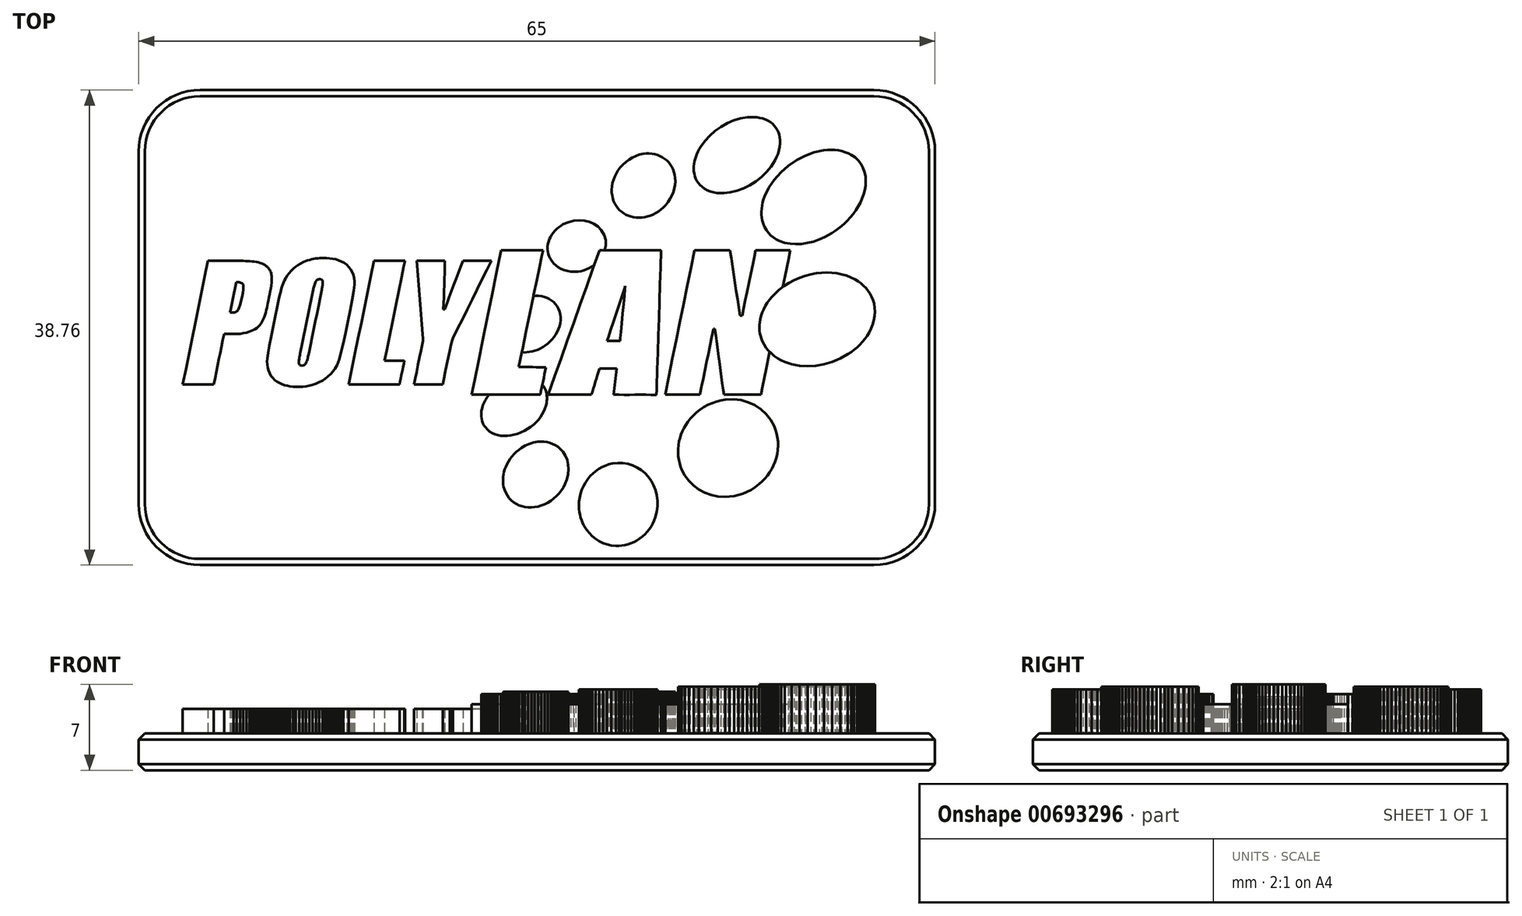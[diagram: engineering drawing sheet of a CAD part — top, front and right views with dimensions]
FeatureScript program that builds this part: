
annotation { "Feature Type Name" : "Feature", "Feature Type Description" : "" }
export const myFeature = defineFeature(function(context is Context, id is Id, definition is map)
    precondition{}
    {
        {
            var Q0;
            Q0=qCreatedBy(makeId("Top.planeOp"),FACE);
            var sketch = newSketch(context, id + "F0", { "sketchPlane" : qUnion([Q0])});
            skLineSegment(sketch, "E0.bottom", {"start": v(-32.5, 0) * mm, "end": v(32.5, 0) * mm});
            skLineSegment(sketch, "E0.top", {"start": v(-32.5, -38.76) * mm, "end": v(32.5, -38.76) * mm});
            skLineSegment(sketch, "E0.left", {"start": v(-32.5, 0) * mm, "end": v(-32.5, -38.76) * mm});
            skLineSegment(sketch, "E0.right", {"start": v(32.5, 0) * mm, "end": v(32.5, -38.76) * mm});
            skSolve(sketch);
        }
        {
            var Q0;
            Q0 = qSketchRegion(id + "F0", true);
            extrude(context, id + "F1", {"entities" : qUnion([Q0]), "depth" : 3 * mm, "offsetDistance" : 25 * mm});
        }
        {
            var Q0;
            Q0=makeQuery(id+"F1.opExtrude","CAP_FACE",FACE,{"disambiguationData":[OSD([sQuery(id+"F0.wireOp",EDGE,"E0.bottom"),sQuery(id+"F0.wireOp",EDGE,"E0.top"),sQuery(id+"F0.wireOp",EDGE,"E0.left"),sQuery(id+"F0.wireOp",EDGE,"E0.right")])],"isStart":false});
            var sketch = newSketch(context, id + "F2", { "sketchPlane" : qUnion([Q0])});
            skLineSegment(sketch, "E1", {"start": v(2.14, -10.96) * mm, "end": v(2.58, -10.77) * mm});
            skLineSegment(sketch, "E2", {"start": v(2.58, -10.77) * mm, "end": v(3.02, -10.66) * mm});
            skLineSegment(sketch, "E3", {"start": v(3.02, -10.66) * mm, "end": v(3.45, -10.62) * mm});
            skLineSegment(sketch, "E4", {"start": v(3.45, -10.62) * mm, "end": v(3.88, -10.66) * mm});
            skLineSegment(sketch, "E5", {"start": v(3.88, -10.66) * mm, "end": v(4.28, -10.76) * mm});
            skLineSegment(sketch, "E6", {"start": v(4.28, -10.76) * mm, "end": v(4.65, -10.92) * mm});
            skLineSegment(sketch, "E7", {"start": v(4.65, -10.92) * mm, "end": v(4.98, -11.14) * mm});
            skLineSegment(sketch, "E8", {"start": v(4.98, -11.14) * mm, "end": v(5.25, -11.42) * mm});
            skLineSegment(sketch, "E9", {"start": v(5.25, -11.42) * mm, "end": v(5.5, -11.83) * mm});
            skLineSegment(sketch, "E10", {"start": v(5.5, -11.83) * mm, "end": v(5.6, -12.25) * mm});
            skLineSegment(sketch, "E11", {"start": v(5.6, -12.25) * mm, "end": v(5.62, -12.68) * mm});
            skLineSegment(sketch, "E12", {"start": v(5.62, -12.68) * mm, "end": v(5.54, -13.1) * mm});
            skLineSegment(sketch, "E13", {"start": v(5.54, -13.1) * mm, "end": v(5.37, -13.49) * mm});
            skLineSegment(sketch, "E14", {"start": v(5.37, -13.49) * mm, "end": v(5.13, -13.85) * mm});
            skLineSegment(sketch, "E15", {"start": v(5.13, -13.85) * mm, "end": v(4.84, -14.16) * mm});
            skLineSegment(sketch, "E16", {"start": v(4.84, -14.16) * mm, "end": v(4.5, -14.4) * mm});
            skLineSegment(sketch, "E17", {"start": v(4.5, -14.4) * mm, "end": v(4.25, -14.54) * mm});
            skLineSegment(sketch, "E18", {"start": v(4.25, -14.54) * mm, "end": v(4.02, -14.64) * mm});
            skLineSegment(sketch, "E19", {"start": v(4.02, -14.64) * mm, "end": v(3.8, -14.72) * mm});
            skLineSegment(sketch, "E20", {"start": v(3.8, -14.72) * mm, "end": v(3.59, -14.77) * mm});
            skLineSegment(sketch, "E21", {"start": v(3.59, -14.77) * mm, "end": v(3.38, -14.8) * mm});
            skLineSegment(sketch, "E22", {"start": v(3.38, -14.8) * mm, "end": v(3.17, -14.82) * mm});
            skLineSegment(sketch, "E23", {"start": v(3.17, -14.82) * mm, "end": v(2.96, -14.82) * mm});
            skLineSegment(sketch, "E24", {"start": v(2.96, -14.82) * mm, "end": v(2.75, -14.8) * mm});
            skLineSegment(sketch, "E25", {"start": v(2.75, -14.8) * mm, "end": v(2.49, -14.76) * mm});
            skLineSegment(sketch, "E26", {"start": v(2.49, -14.76) * mm, "end": v(2.23, -14.68) * mm});
            skLineSegment(sketch, "E27", {"start": v(2.23, -14.68) * mm, "end": v(1.99, -14.59) * mm});
            skLineSegment(sketch, "E28", {"start": v(1.99, -14.59) * mm, "end": v(1.76, -14.46) * mm});
            skLineSegment(sketch, "E29", {"start": v(1.76, -14.46) * mm, "end": v(1.55, -14.31) * mm});
            skLineSegment(sketch, "E30", {"start": v(1.55, -14.31) * mm, "end": v(1.37, -14.14) * mm});
            skLineSegment(sketch, "E31", {"start": v(1.37, -14.14) * mm, "end": v(1.2, -13.94) * mm});
            skLineSegment(sketch, "E32", {"start": v(1.2, -13.94) * mm, "end": v(1.07, -13.73) * mm});
            skLineSegment(sketch, "E33", {"start": v(1.07, -13.73) * mm, "end": v(1, -13.55) * mm});
            skLineSegment(sketch, "E34", {"start": v(1, -13.55) * mm, "end": v(0.93, -13.37) * mm});
            skLineSegment(sketch, "E35", {"start": v(0.93, -13.37) * mm, "end": v(0.89, -13.18) * mm});
            skLineSegment(sketch, "E36", {"start": v(0.89, -13.18) * mm, "end": v(0.87, -12.98) * mm});
            skLineSegment(sketch, "E37", {"start": v(0.87, -12.98) * mm, "end": v(0.87, -12.78) * mm});
            skLineSegment(sketch, "E38", {"start": v(0.87, -12.78) * mm, "end": v(0.9, -12.58) * mm});
            skLineSegment(sketch, "E39", {"start": v(0.9, -12.58) * mm, "end": v(0.94, -12.37) * mm});
            skLineSegment(sketch, "E40", {"start": v(0.94, -12.37) * mm, "end": v(1.02, -12.17) * mm});
            skLineSegment(sketch, "E41", {"start": v(1.02, -12.17) * mm, "end": v(1.1, -11.98) * mm});
            skLineSegment(sketch, "E42", {"start": v(1.1, -11.98) * mm, "end": v(1.2, -11.8) * mm});
            skLineSegment(sketch, "E43", {"start": v(1.2, -11.8) * mm, "end": v(1.33, -11.63) * mm});
            skLineSegment(sketch, "E44", {"start": v(1.33, -11.63) * mm, "end": v(1.47, -11.47) * mm});
            skLineSegment(sketch, "E45", {"start": v(1.47, -11.47) * mm, "end": v(1.62, -11.32) * mm});
            skLineSegment(sketch, "E46", {"start": v(1.62, -11.32) * mm, "end": v(1.79, -11.19) * mm});
            skLineSegment(sketch, "E47", {"start": v(1.79, -11.19) * mm, "end": v(1.96, -11.06) * mm});
            skLineSegment(sketch, "E48", {"start": v(1.96, -11.06) * mm, "end": v(2.14, -10.96) * mm});
            skLineSegment(sketch, "E49", {"start": v(-0.1, -16.78) * mm, "end": v(0.14, -16.8) * mm});
            skLineSegment(sketch, "E50", {"start": v(0.14, -16.8) * mm, "end": v(0.37, -16.83) * mm});
            skLineSegment(sketch, "E51", {"start": v(0.37, -16.83) * mm, "end": v(0.6, -16.88) * mm});
            skLineSegment(sketch, "E52", {"start": v(0.6, -16.88) * mm, "end": v(0.8, -16.96) * mm});
            skLineSegment(sketch, "E53", {"start": v(0.8, -16.96) * mm, "end": v(1, -17.06) * mm});
            skLineSegment(sketch, "E54", {"start": v(1, -17.06) * mm, "end": v(1.19, -17.17) * mm});
            skLineSegment(sketch, "E55", {"start": v(1.19, -17.17) * mm, "end": v(1.36, -17.3) * mm});
            skLineSegment(sketch, "E56", {"start": v(1.36, -17.3) * mm, "end": v(1.5, -17.47) * mm});
            skLineSegment(sketch, "E57", {"start": v(1.5, -17.47) * mm, "end": v(1.65, -17.65) * mm});
            skLineSegment(sketch, "E58", {"start": v(1.65, -17.65) * mm, "end": v(1.76, -17.85) * mm});
            skLineSegment(sketch, "E59", {"start": v(1.76, -17.85) * mm, "end": v(1.84, -18.07) * mm});
            skLineSegment(sketch, "E60", {"start": v(1.84, -18.07) * mm, "end": v(1.9, -18.3) * mm});
            skLineSegment(sketch, "E61", {"start": v(1.9, -18.3) * mm, "end": v(1.93, -18.54) * mm});
            skLineSegment(sketch, "E62", {"start": v(1.93, -18.54) * mm, "end": v(1.93, -18.78) * mm});
            skLineSegment(sketch, "E63", {"start": v(1.93, -18.78) * mm, "end": v(1.9, -19.04) * mm});
            skLineSegment(sketch, "E64", {"start": v(1.9, -19.04) * mm, "end": v(1.84, -19.29) * mm});
            skLineSegment(sketch, "E65", {"start": v(1.84, -19.29) * mm, "end": v(1.77, -19.51) * mm});
            skLineSegment(sketch, "E66", {"start": v(1.77, -19.51) * mm, "end": v(1.67, -19.74) * mm});
            skLineSegment(sketch, "E67", {"start": v(1.67, -19.74) * mm, "end": v(1.54, -19.95) * mm});
            skLineSegment(sketch, "E68", {"start": v(1.54, -19.95) * mm, "end": v(1.4, -20.15) * mm});
            skLineSegment(sketch, "E69", {"start": v(1.4, -20.15) * mm, "end": v(1.24, -20.35) * mm});
            skLineSegment(sketch, "E70", {"start": v(1.24, -20.35) * mm, "end": v(1.07, -20.53) * mm});
            skLineSegment(sketch, "E71", {"start": v(1.07, -20.53) * mm, "end": v(0.88, -20.7) * mm});
            skLineSegment(sketch, "E72", {"start": v(0.88, -20.7) * mm, "end": v(0.68, -20.85) * mm});
            skLineSegment(sketch, "E73", {"start": v(0.68, -20.85) * mm, "end": v(0.48, -20.98) * mm});
            skLineSegment(sketch, "E74", {"start": v(0.48, -20.98) * mm, "end": v(0.27, -21.1) * mm});
            skLineSegment(sketch, "E75", {"start": v(0.27, -21.1) * mm, "end": v(0.06, -21.19) * mm});
            skLineSegment(sketch, "E76", {"start": v(0.06, -21.19) * mm, "end": v(-0.16, -21.27) * mm});
            skLineSegment(sketch, "E77", {"start": v(-0.16, -21.27) * mm, "end": v(-0.38, -21.33) * mm});
            skLineSegment(sketch, "E78", {"start": v(-0.38, -21.33) * mm, "end": v(-0.6, -21.37) * mm});
            skLineSegment(sketch, "E79", {"start": v(-0.6, -21.37) * mm, "end": v(-0.82, -21.4) * mm});
            skLineSegment(sketch, "E80", {"start": v(-0.82, -21.4) * mm, "end": v(-1.04, -21.41) * mm});
            skLineSegment(sketch, "E81", {"start": v(-1.04, -21.41) * mm, "end": v(-2.2, -21.3) * mm});
            skLineSegment(sketch, "E82", {"start": v(-2.2, -21.3) * mm, "end": v(-2.99, -20.8) * mm});
            skLineSegment(sketch, "E83", {"start": v(-2.99, -20.8) * mm, "end": v(-3.4, -20.08) * mm});
            skLineSegment(sketch, "E84", {"start": v(-3.4, -20.08) * mm, "end": v(-3.43, -19.23) * mm});
            skLineSegment(sketch, "E85", {"start": v(-3.43, -19.23) * mm, "end": v(-3.12, -18.35) * mm});
            skLineSegment(sketch, "E86", {"start": v(-3.12, -18.35) * mm, "end": v(-2.45, -17.58) * mm});
            skLineSegment(sketch, "E87", {"start": v(-2.45, -17.58) * mm, "end": v(-1.44, -17.02) * mm});
            skLineSegment(sketch, "E88", {"start": v(-1.44, -17.02) * mm, "end": v(-0.1, -16.78) * mm});
            skLineSegment(sketch, "E89", {"start": v(0.68, -24.4) * mm, "end": v(0.73, -24.52) * mm});
            skLineSegment(sketch, "E90", {"start": v(0.73, -24.52) * mm, "end": v(0.77, -24.65) * mm});
            skLineSegment(sketch, "E91", {"start": v(0.77, -24.65) * mm, "end": v(0.8, -24.79) * mm});
            skLineSegment(sketch, "E92", {"start": v(0.8, -24.79) * mm, "end": v(0.81, -24.93) * mm});
            skLineSegment(sketch, "E93", {"start": v(0.81, -24.93) * mm, "end": v(0.82, -25.08) * mm});
            skLineSegment(sketch, "E94", {"start": v(0.82, -25.08) * mm, "end": v(0.82, -25.23) * mm});
            skLineSegment(sketch, "E95", {"start": v(0.82, -25.23) * mm, "end": v(0.8, -25.38) * mm});
            skLineSegment(sketch, "E96", {"start": v(0.8, -25.38) * mm, "end": v(0.79, -25.54) * mm});
            skLineSegment(sketch, "E97", {"start": v(0.79, -25.54) * mm, "end": v(0.73, -25.78) * mm});
            skLineSegment(sketch, "E98", {"start": v(0.73, -25.78) * mm, "end": v(0.65, -26.02) * mm});
            skLineSegment(sketch, "E99", {"start": v(0.65, -26.02) * mm, "end": v(0.55, -26.25) * mm});
            skLineSegment(sketch, "E100", {"start": v(0.55, -26.25) * mm, "end": v(0.43, -26.48) * mm});
            skLineSegment(sketch, "E101", {"start": v(0.43, -26.48) * mm, "end": v(0.28, -26.7) * mm});
            skLineSegment(sketch, "E102", {"start": v(0.28, -26.7) * mm, "end": v(0.12, -26.91) * mm});
            skLineSegment(sketch, "E103", {"start": v(0.12, -26.91) * mm, "end": v(-0.06, -27.1) * mm});
            skLineSegment(sketch, "E104", {"start": v(-0.06, -27.1) * mm, "end": v(-0.26, -27.29) * mm});
            skLineSegment(sketch, "E105", {"start": v(-0.26, -27.29) * mm, "end": v(-0.5, -27.48) * mm});
            skLineSegment(sketch, "E106", {"start": v(-0.5, -27.48) * mm, "end": v(-0.75, -27.66) * mm});
            skLineSegment(sketch, "E107", {"start": v(-0.75, -27.66) * mm, "end": v(-1.02, -27.81) * mm});
            skLineSegment(sketch, "E108", {"start": v(-1.02, -27.81) * mm, "end": v(-1.3, -27.94) * mm});
            skLineSegment(sketch, "E109", {"start": v(-1.3, -27.94) * mm, "end": v(-1.57, -28.05) * mm});
            skLineSegment(sketch, "E110", {"start": v(-1.57, -28.05) * mm, "end": v(-1.85, -28.13) * mm});
            skLineSegment(sketch, "E111", {"start": v(-1.85, -28.13) * mm, "end": v(-2.14, -28.19) * mm});
            skLineSegment(sketch, "E112", {"start": v(-2.14, -28.19) * mm, "end": v(-2.42, -28.22) * mm});
            skLineSegment(sketch, "E113", {"start": v(-2.42, -28.22) * mm, "end": v(-2.68, -28.22) * mm});
            skLineSegment(sketch, "E114", {"start": v(-2.68, -28.22) * mm, "end": v(-2.94, -28.2) * mm});
            skLineSegment(sketch, "E115", {"start": v(-2.94, -28.2) * mm, "end": v(-3.2, -28.16) * mm});
            skLineSegment(sketch, "E116", {"start": v(-3.2, -28.16) * mm, "end": v(-3.43, -28.08) * mm});
            skLineSegment(sketch, "E117", {"start": v(-3.43, -28.08) * mm, "end": v(-3.65, -27.98) * mm});
            skLineSegment(sketch, "E118", {"start": v(-3.65, -27.98) * mm, "end": v(-3.86, -27.86) * mm});
            skLineSegment(sketch, "E119", {"start": v(-3.86, -27.86) * mm, "end": v(-4.04, -27.71) * mm});
            skLineSegment(sketch, "E120", {"start": v(-4.04, -27.71) * mm, "end": v(-4.2, -27.53) * mm});
            skLineSegment(sketch, "E121", {"start": v(-4.2, -27.53) * mm, "end": v(-4.31, -27.38) * mm});
            skLineSegment(sketch, "E122", {"start": v(-4.31, -27.38) * mm, "end": v(-4.4, -27.2) * mm});
            skLineSegment(sketch, "E123", {"start": v(-4.4, -27.2) * mm, "end": v(-4.47, -27.02) * mm});
            skLineSegment(sketch, "E124", {"start": v(-4.47, -27.02) * mm, "end": v(-4.52, -26.82) * mm});
            skLineSegment(sketch, "E125", {"start": v(-4.52, -26.82) * mm, "end": v(-4.54, -26.62) * mm});
            skLineSegment(sketch, "E126", {"start": v(-4.54, -26.62) * mm, "end": v(-4.54, -26.4) * mm});
            skLineSegment(sketch, "E127", {"start": v(-4.54, -26.4) * mm, "end": v(-4.52, -26.2) * mm});
            skLineSegment(sketch, "E128", {"start": v(-4.52, -26.2) * mm, "end": v(-4.48, -25.98) * mm});
            skLineSegment(sketch, "E129", {"start": v(-4.48, -25.98) * mm, "end": v(-4.44, -25.85) * mm});
            skLineSegment(sketch, "E130", {"start": v(-4.44, -25.85) * mm, "end": v(-4.4, -25.72) * mm});
            skLineSegment(sketch, "E131", {"start": v(-4.4, -25.72) * mm, "end": v(-4.35, -25.6) * mm});
            skLineSegment(sketch, "E132", {"start": v(-4.35, -25.6) * mm, "end": v(-4.29, -25.47) * mm});
            skLineSegment(sketch, "E133", {"start": v(-4.29, -25.47) * mm, "end": v(-4.22, -25.34) * mm});
            skLineSegment(sketch, "E134", {"start": v(-4.22, -25.34) * mm, "end": v(-4.15, -25.22) * mm});
            skLineSegment(sketch, "E135", {"start": v(-4.15, -25.22) * mm, "end": v(-4.08, -25.1) * mm});
            skLineSegment(sketch, "E136", {"start": v(-4.08, -25.1) * mm, "end": v(-4, -24.98) * mm});
            skLineSegment(sketch, "E137", {"start": v(-4, -24.98) * mm, "end": v(-3.7, -24.66) * mm});
            skLineSegment(sketch, "E138", {"start": v(-3.7, -24.66) * mm, "end": v(-3.35, -24.37) * mm});
            skLineSegment(sketch, "E139", {"start": v(-3.35, -24.37) * mm, "end": v(-3, -24.13) * mm});
            skLineSegment(sketch, "E140", {"start": v(-3, -24.13) * mm, "end": v(-2.64, -23.92) * mm});
            skLineSegment(sketch, "E141", {"start": v(-2.64, -23.92) * mm, "end": v(-2.28, -23.76) * mm});
            skLineSegment(sketch, "E142", {"start": v(-2.28, -23.76) * mm, "end": v(-1.95, -23.64) * mm});
            skLineSegment(sketch, "E143", {"start": v(-1.95, -23.64) * mm, "end": v(-1.66, -23.57) * mm});
            skLineSegment(sketch, "E144", {"start": v(-1.66, -23.57) * mm, "end": v(-1.4, -23.55) * mm});
            skLineSegment(sketch, "E145", {"start": v(-1.4, -23.55) * mm, "end": v(-0.8, -23.57) * mm});
            skLineSegment(sketch, "E146", {"start": v(-0.8, -23.57) * mm, "end": v(-0.33, -23.64) * mm});
            skLineSegment(sketch, "E147", {"start": v(-0.33, -23.64) * mm, "end": v(0.02, -23.74) * mm});
            skLineSegment(sketch, "E148", {"start": v(0.02, -23.74) * mm, "end": v(0.26, -23.87) * mm});
            skLineSegment(sketch, "E149", {"start": v(0.26, -23.87) * mm, "end": v(0.42, -24) * mm});
            skLineSegment(sketch, "E150", {"start": v(0.42, -24) * mm, "end": v(0.53, -24.15) * mm});
            skLineSegment(sketch, "E151", {"start": v(0.53, -24.15) * mm, "end": v(0.61, -24.28) * mm});
            skLineSegment(sketch, "E152", {"start": v(0.61, -24.28) * mm, "end": v(0.68, -24.4) * mm});
            skLineSegment(sketch, "E153", {"start": v(17.17, -2.22) * mm, "end": v(17.43, -2.2) * mm});
            skLineSegment(sketch, "E154", {"start": v(17.43, -2.2) * mm, "end": v(17.7, -2.2) * mm});
            skLineSegment(sketch, "E155", {"start": v(17.7, -2.2) * mm, "end": v(17.95, -2.22) * mm});
            skLineSegment(sketch, "E156", {"start": v(17.95, -2.22) * mm, "end": v(18.2, -2.26) * mm});
            skLineSegment(sketch, "E157", {"start": v(18.2, -2.26) * mm, "end": v(18.43, -2.32) * mm});
            skLineSegment(sketch, "E158", {"start": v(18.43, -2.32) * mm, "end": v(18.66, -2.4) * mm});
            skLineSegment(sketch, "E159", {"start": v(18.66, -2.4) * mm, "end": v(18.88, -2.51) * mm});
            skLineSegment(sketch, "E160", {"start": v(18.88, -2.51) * mm, "end": v(19.08, -2.64) * mm});
            skLineSegment(sketch, "E161", {"start": v(19.08, -2.64) * mm, "end": v(19.24, -2.77) * mm});
            skLineSegment(sketch, "E162", {"start": v(19.24, -2.77) * mm, "end": v(19.38, -2.92) * mm});
            skLineSegment(sketch, "E163", {"start": v(19.38, -2.92) * mm, "end": v(19.51, -3.08) * mm});
            skLineSegment(sketch, "E164", {"start": v(19.51, -3.08) * mm, "end": v(19.62, -3.26) * mm});
            skLineSegment(sketch, "E165", {"start": v(19.62, -3.26) * mm, "end": v(19.71, -3.45) * mm});
            skLineSegment(sketch, "E166", {"start": v(19.71, -3.45) * mm, "end": v(19.78, -3.65) * mm});
            skLineSegment(sketch, "E167", {"start": v(19.78, -3.65) * mm, "end": v(19.83, -3.86) * mm});
            skLineSegment(sketch, "E168", {"start": v(19.83, -3.86) * mm, "end": v(19.85, -4.08) * mm});
            skLineSegment(sketch, "E169", {"start": v(19.85, -4.08) * mm, "end": v(19.85, -4.35) * mm});
            skLineSegment(sketch, "E170", {"start": v(19.85, -4.35) * mm, "end": v(19.82, -4.63) * mm});
            skLineSegment(sketch, "E171", {"start": v(19.82, -4.63) * mm, "end": v(19.76, -4.91) * mm});
            skLineSegment(sketch, "E172", {"start": v(19.76, -4.91) * mm, "end": v(19.68, -5.2) * mm});
            skLineSegment(sketch, "E173", {"start": v(19.68, -5.2) * mm, "end": v(19.57, -5.47) * mm});
            skLineSegment(sketch, "E174", {"start": v(19.57, -5.47) * mm, "end": v(19.43, -5.74) * mm});
            skLineSegment(sketch, "E175", {"start": v(19.43, -5.74) * mm, "end": v(19.28, -6) * mm});
            skLineSegment(sketch, "E176", {"start": v(19.28, -6) * mm, "end": v(19.1, -6.25) * mm});
            skLineSegment(sketch, "E177", {"start": v(19.1, -6.25) * mm, "end": v(18.74, -6.7) * mm});
            skLineSegment(sketch, "E178", {"start": v(18.74, -6.7) * mm, "end": v(18.32, -7.1) * mm});
            skLineSegment(sketch, "E179", {"start": v(18.32, -7.1) * mm, "end": v(17.86, -7.46) * mm});
            skLineSegment(sketch, "E180", {"start": v(17.86, -7.46) * mm, "end": v(17.37, -7.77) * mm});
            skLineSegment(sketch, "E181", {"start": v(17.37, -7.77) * mm, "end": v(16.86, -8.03) * mm});
            skLineSegment(sketch, "E182", {"start": v(16.86, -8.03) * mm, "end": v(16.33, -8.22) * mm});
            skLineSegment(sketch, "E183", {"start": v(16.33, -8.22) * mm, "end": v(15.8, -8.35) * mm});
            skLineSegment(sketch, "E184", {"start": v(15.8, -8.35) * mm, "end": v(15.26, -8.42) * mm});
            skLineSegment(sketch, "E185", {"start": v(15.26, -8.42) * mm, "end": v(14.98, -8.42) * mm});
            skLineSegment(sketch, "E186", {"start": v(14.98, -8.42) * mm, "end": v(14.7, -8.4) * mm});
            skLineSegment(sketch, "E187", {"start": v(14.7, -8.4) * mm, "end": v(14.43, -8.35) * mm});
            skLineSegment(sketch, "E188", {"start": v(14.43, -8.35) * mm, "end": v(14.17, -8.28) * mm});
            skLineSegment(sketch, "E189", {"start": v(14.17, -8.28) * mm, "end": v(13.92, -8.18) * mm});
            skLineSegment(sketch, "E190", {"start": v(13.92, -8.18) * mm, "end": v(13.7, -8.06) * mm});
            skLineSegment(sketch, "E191", {"start": v(13.7, -8.06) * mm, "end": v(13.48, -7.9) * mm});
            skLineSegment(sketch, "E192", {"start": v(13.48, -7.9) * mm, "end": v(13.3, -7.73) * mm});
            skLineSegment(sketch, "E193", {"start": v(13.3, -7.73) * mm, "end": v(13.17, -7.58) * mm});
            skLineSegment(sketch, "E194", {"start": v(13.17, -7.58) * mm, "end": v(13.06, -7.41) * mm});
            skLineSegment(sketch, "E195", {"start": v(13.06, -7.41) * mm, "end": v(12.97, -7.23) * mm});
            skLineSegment(sketch, "E196", {"start": v(12.97, -7.23) * mm, "end": v(12.9, -7.04) * mm});
            skLineSegment(sketch, "E197", {"start": v(12.9, -7.04) * mm, "end": v(12.85, -6.85) * mm});
            skLineSegment(sketch, "E198", {"start": v(12.85, -6.85) * mm, "end": v(12.81, -6.64) * mm});
            skLineSegment(sketch, "E199", {"start": v(12.81, -6.64) * mm, "end": v(12.8, -6.43) * mm});
            skLineSegment(sketch, "E200", {"start": v(12.8, -6.43) * mm, "end": v(12.8, -6.21) * mm});
            skLineSegment(sketch, "E201", {"start": v(12.8, -6.21) * mm, "end": v(12.83, -6.01) * mm});
            skLineSegment(sketch, "E202", {"start": v(12.83, -6.01) * mm, "end": v(12.86, -5.81) * mm});
            skLineSegment(sketch, "E203", {"start": v(12.86, -5.81) * mm, "end": v(12.92, -5.61) * mm});
            skLineSegment(sketch, "E204", {"start": v(12.92, -5.61) * mm, "end": v(12.98, -5.41) * mm});
            skLineSegment(sketch, "E205", {"start": v(12.98, -5.41) * mm, "end": v(13.06, -5.21) * mm});
            skLineSegment(sketch, "E206", {"start": v(13.06, -5.21) * mm, "end": v(13.15, -5.02) * mm});
            skLineSegment(sketch, "E207", {"start": v(13.15, -5.02) * mm, "end": v(13.25, -4.83) * mm});
            skLineSegment(sketch, "E208", {"start": v(13.25, -4.83) * mm, "end": v(13.36, -4.64) * mm});
            skLineSegment(sketch, "E209", {"start": v(13.36, -4.64) * mm, "end": v(13.7, -4.16) * mm});
            skLineSegment(sketch, "E210", {"start": v(13.7, -4.16) * mm, "end": v(14.1, -3.73) * mm});
            skLineSegment(sketch, "E211", {"start": v(14.1, -3.73) * mm, "end": v(14.55, -3.34) * mm});
            skLineSegment(sketch, "E212", {"start": v(14.55, -3.34) * mm, "end": v(15.04, -3) * mm});
            skLineSegment(sketch, "E213", {"start": v(15.04, -3) * mm, "end": v(15.55, -2.7) * mm});
            skLineSegment(sketch, "E214", {"start": v(15.55, -2.7) * mm, "end": v(16.08, -2.48) * mm});
            skLineSegment(sketch, "E215", {"start": v(16.08, -2.48) * mm, "end": v(16.63, -2.31) * mm});
            skLineSegment(sketch, "E216", {"start": v(16.63, -2.31) * mm, "end": v(17.17, -2.22) * mm});
            skLineSegment(sketch, "E217", {"start": v(23.4, -4.92) * mm, "end": v(23.7, -4.89) * mm});
            skLineSegment(sketch, "E218", {"start": v(23.7, -4.89) * mm, "end": v(24.01, -4.88) * mm});
            skLineSegment(sketch, "E219", {"start": v(24.01, -4.88) * mm, "end": v(24.31, -4.9) * mm});
            skLineSegment(sketch, "E220", {"start": v(24.31, -4.9) * mm, "end": v(24.6, -4.93) * mm});
            skLineSegment(sketch, "E221", {"start": v(24.6, -4.93) * mm, "end": v(24.89, -4.98) * mm});
            skLineSegment(sketch, "E222", {"start": v(24.89, -4.98) * mm, "end": v(25.16, -5.06) * mm});
            skLineSegment(sketch, "E223", {"start": v(25.16, -5.06) * mm, "end": v(25.43, -5.17) * mm});
            skLineSegment(sketch, "E224", {"start": v(25.43, -5.17) * mm, "end": v(25.67, -5.3) * mm});
            skLineSegment(sketch, "E225", {"start": v(25.67, -5.3) * mm, "end": v(25.97, -5.5) * mm});
            skLineSegment(sketch, "E226", {"start": v(25.97, -5.5) * mm, "end": v(26.22, -5.74) * mm});
            skLineSegment(sketch, "E227", {"start": v(26.22, -5.74) * mm, "end": v(26.44, -6.02) * mm});
            skLineSegment(sketch, "E228", {"start": v(26.44, -6.02) * mm, "end": v(26.61, -6.34) * mm});
            skLineSegment(sketch, "E229", {"start": v(26.61, -6.34) * mm, "end": v(26.74, -6.68) * mm});
            skLineSegment(sketch, "E230", {"start": v(26.74, -6.68) * mm, "end": v(26.82, -7.04) * mm});
            skLineSegment(sketch, "E231", {"start": v(26.82, -7.04) * mm, "end": v(26.85, -7.41) * mm});
            skLineSegment(sketch, "E232", {"start": v(26.85, -7.41) * mm, "end": v(26.82, -7.8) * mm});
            skLineSegment(sketch, "E233", {"start": v(26.82, -7.8) * mm, "end": v(26.77, -8.15) * mm});
            skLineSegment(sketch, "E234", {"start": v(26.77, -8.15) * mm, "end": v(26.68, -8.5) * mm});
            skLineSegment(sketch, "E235", {"start": v(26.68, -8.5) * mm, "end": v(26.56, -8.83) * mm});
            skLineSegment(sketch, "E236", {"start": v(26.56, -8.83) * mm, "end": v(26.4, -9.17) * mm});
            skLineSegment(sketch, "E237", {"start": v(26.4, -9.17) * mm, "end": v(26.23, -9.5) * mm});
            skLineSegment(sketch, "E238", {"start": v(26.23, -9.5) * mm, "end": v(26.03, -9.81) * mm});
            skLineSegment(sketch, "E239", {"start": v(26.03, -9.81) * mm, "end": v(25.81, -10.12) * mm});
            skLineSegment(sketch, "E240", {"start": v(25.81, -10.12) * mm, "end": v(25.57, -10.41) * mm});
            skLineSegment(sketch, "E241", {"start": v(25.57, -10.41) * mm, "end": v(25.35, -10.65) * mm});
            skLineSegment(sketch, "E242", {"start": v(25.35, -10.65) * mm, "end": v(25.11, -10.88) * mm});
            skLineSegment(sketch, "E243", {"start": v(25.11, -10.88) * mm, "end": v(24.87, -11.1) * mm});
            skLineSegment(sketch, "E244", {"start": v(24.87, -11.1) * mm, "end": v(24.61, -11.3) * mm});
            skLineSegment(sketch, "E245", {"start": v(24.61, -11.3) * mm, "end": v(24.35, -11.5) * mm});
            skLineSegment(sketch, "E246", {"start": v(24.35, -11.5) * mm, "end": v(24.07, -11.67) * mm});
            skLineSegment(sketch, "E247", {"start": v(24.07, -11.67) * mm, "end": v(23.8, -11.84) * mm});
            skLineSegment(sketch, "E248", {"start": v(23.8, -11.84) * mm, "end": v(23.5, -11.99) * mm});
            skLineSegment(sketch, "E249", {"start": v(23.5, -11.99) * mm, "end": v(23.04, -12.2) * mm});
            skLineSegment(sketch, "E250", {"start": v(23.04, -12.2) * mm, "end": v(22.57, -12.36) * mm});
            skLineSegment(sketch, "E251", {"start": v(22.57, -12.36) * mm, "end": v(22.08, -12.48) * mm});
            skLineSegment(sketch, "E252", {"start": v(22.08, -12.48) * mm, "end": v(21.6, -12.55) * mm});
            skLineSegment(sketch, "E253", {"start": v(21.6, -12.55) * mm, "end": v(21.13, -12.57) * mm});
            skLineSegment(sketch, "E254", {"start": v(21.13, -12.57) * mm, "end": v(20.66, -12.54) * mm});
            skLineSegment(sketch, "E255", {"start": v(20.66, -12.54) * mm, "end": v(20.22, -12.46) * mm});
            skLineSegment(sketch, "E256", {"start": v(20.22, -12.46) * mm, "end": v(19.8, -12.31) * mm});
            skLineSegment(sketch, "E257", {"start": v(19.8, -12.31) * mm, "end": v(19.54, -12.18) * mm});
            skLineSegment(sketch, "E258", {"start": v(19.54, -12.18) * mm, "end": v(19.3, -12.03) * mm});
            skLineSegment(sketch, "E259", {"start": v(19.3, -12.03) * mm, "end": v(19.09, -11.85) * mm});
            skLineSegment(sketch, "E260", {"start": v(19.09, -11.85) * mm, "end": v(18.9, -11.65) * mm});
            skLineSegment(sketch, "E261", {"start": v(18.9, -11.65) * mm, "end": v(18.72, -11.42) * mm});
            skLineSegment(sketch, "E262", {"start": v(18.72, -11.42) * mm, "end": v(18.58, -11.18) * mm});
            skLineSegment(sketch, "E263", {"start": v(18.58, -11.18) * mm, "end": v(18.47, -10.92) * mm});
            skLineSegment(sketch, "E264", {"start": v(18.47, -10.92) * mm, "end": v(18.4, -10.64) * mm});
            skLineSegment(sketch, "E265", {"start": v(18.4, -10.64) * mm, "end": v(18.35, -10.4) * mm});
            skLineSegment(sketch, "E266", {"start": v(18.35, -10.4) * mm, "end": v(18.32, -10.17) * mm});
            skLineSegment(sketch, "E267", {"start": v(18.32, -10.17) * mm, "end": v(18.32, -9.92) * mm});
            skLineSegment(sketch, "E268", {"start": v(18.32, -9.92) * mm, "end": v(18.34, -9.68) * mm});
            skLineSegment(sketch, "E269", {"start": v(18.34, -9.68) * mm, "end": v(18.38, -9.43) * mm});
            skLineSegment(sketch, "E270", {"start": v(18.38, -9.43) * mm, "end": v(18.43, -9.18) * mm});
            skLineSegment(sketch, "E271", {"start": v(18.43, -9.18) * mm, "end": v(18.5, -8.93) * mm});
            skLineSegment(sketch, "E272", {"start": v(18.5, -8.93) * mm, "end": v(18.58, -8.69) * mm});
            skLineSegment(sketch, "E273", {"start": v(18.58, -8.69) * mm, "end": v(18.92, -7.97) * mm});
            skLineSegment(sketch, "E274", {"start": v(18.92, -7.97) * mm, "end": v(19.37, -7.31) * mm});
            skLineSegment(sketch, "E275", {"start": v(19.37, -7.31) * mm, "end": v(19.91, -6.7) * mm});
            skLineSegment(sketch, "E276", {"start": v(19.91, -6.7) * mm, "end": v(20.52, -6.17) * mm});
            skLineSegment(sketch, "E277", {"start": v(20.52, -6.17) * mm, "end": v(21.2, -5.71) * mm});
            skLineSegment(sketch, "E278", {"start": v(21.2, -5.71) * mm, "end": v(21.91, -5.35) * mm});
            skLineSegment(sketch, "E279", {"start": v(21.91, -5.35) * mm, "end": v(22.65, -5.08) * mm});
            skLineSegment(sketch, "E280", {"start": v(22.65, -5.08) * mm, "end": v(23.4, -4.92) * mm});
            skLineSegment(sketch, "E281", {"start": v(8.67, -5.21) * mm, "end": v(8.91, -5.18) * mm});
            skLineSegment(sketch, "E282", {"start": v(8.91, -5.18) * mm, "end": v(9.15, -5.18) * mm});
            skLineSegment(sketch, "E283", {"start": v(9.15, -5.18) * mm, "end": v(9.39, -5.2) * mm});
            skLineSegment(sketch, "E284", {"start": v(9.39, -5.2) * mm, "end": v(9.62, -5.23) * mm});
            skLineSegment(sketch, "E285", {"start": v(9.62, -5.23) * mm, "end": v(9.84, -5.3) * mm});
            skLineSegment(sketch, "E286", {"start": v(9.84, -5.3) * mm, "end": v(10.04, -5.38) * mm});
            skLineSegment(sketch, "E287", {"start": v(10.04, -5.38) * mm, "end": v(10.24, -5.48) * mm});
            skLineSegment(sketch, "E288", {"start": v(10.24, -5.48) * mm, "end": v(10.42, -5.6) * mm});
            skLineSegment(sketch, "E289", {"start": v(10.42, -5.6) * mm, "end": v(10.6, -5.74) * mm});
            skLineSegment(sketch, "E290", {"start": v(10.6, -5.74) * mm, "end": v(10.76, -5.9) * mm});
            skLineSegment(sketch, "E291", {"start": v(10.76, -5.9) * mm, "end": v(10.9, -6.08) * mm});
            skLineSegment(sketch, "E292", {"start": v(10.9, -6.08) * mm, "end": v(11.02, -6.28) * mm});
            skLineSegment(sketch, "E293", {"start": v(11.02, -6.28) * mm, "end": v(11.12, -6.48) * mm});
            skLineSegment(sketch, "E294", {"start": v(11.12, -6.48) * mm, "end": v(11.2, -6.7) * mm});
            skLineSegment(sketch, "E295", {"start": v(11.2, -6.7) * mm, "end": v(11.25, -6.93) * mm});
            skLineSegment(sketch, "E296", {"start": v(11.25, -6.93) * mm, "end": v(11.29, -7.17) * mm});
            skLineSegment(sketch, "E297", {"start": v(11.29, -7.17) * mm, "end": v(11.3, -7.45) * mm});
            skLineSegment(sketch, "E298", {"start": v(11.3, -7.45) * mm, "end": v(11.28, -7.74) * mm});
            skLineSegment(sketch, "E299", {"start": v(11.28, -7.74) * mm, "end": v(11.23, -8.03) * mm});
            skLineSegment(sketch, "E300", {"start": v(11.23, -8.03) * mm, "end": v(11.14, -8.32) * mm});
            skLineSegment(sketch, "E301", {"start": v(11.14, -8.32) * mm, "end": v(11.02, -8.6) * mm});
            skLineSegment(sketch, "E302", {"start": v(11.02, -8.6) * mm, "end": v(10.88, -8.88) * mm});
            skLineSegment(sketch, "E303", {"start": v(10.88, -8.88) * mm, "end": v(10.7, -9.15) * mm});
            skLineSegment(sketch, "E304", {"start": v(10.7, -9.15) * mm, "end": v(10.5, -9.4) * mm});
            skLineSegment(sketch, "E305", {"start": v(10.5, -9.4) * mm, "end": v(10.32, -9.58) * mm});
            skLineSegment(sketch, "E306", {"start": v(10.32, -9.58) * mm, "end": v(10.13, -9.74) * mm});
            skLineSegment(sketch, "E307", {"start": v(10.13, -9.74) * mm, "end": v(9.93, -9.9) * mm});
            skLineSegment(sketch, "E308", {"start": v(9.93, -9.9) * mm, "end": v(9.71, -10.03) * mm});
            skLineSegment(sketch, "E309", {"start": v(9.71, -10.03) * mm, "end": v(9.5, -10.14) * mm});
            skLineSegment(sketch, "E310", {"start": v(9.5, -10.14) * mm, "end": v(9.26, -10.24) * mm});
            skLineSegment(sketch, "E311", {"start": v(9.26, -10.24) * mm, "end": v(9.03, -10.32) * mm});
            skLineSegment(sketch, "E312", {"start": v(9.03, -10.32) * mm, "end": v(8.8, -10.37) * mm});
            skLineSegment(sketch, "E313", {"start": v(8.8, -10.37) * mm, "end": v(8.57, -10.4) * mm});
            skLineSegment(sketch, "E314", {"start": v(8.57, -10.4) * mm, "end": v(8.33, -10.41) * mm});
            skLineSegment(sketch, "E315", {"start": v(8.33, -10.41) * mm, "end": v(8.1, -10.4) * mm});
            skLineSegment(sketch, "E316", {"start": v(8.1, -10.4) * mm, "end": v(7.88, -10.37) * mm});
            skLineSegment(sketch, "E317", {"start": v(7.88, -10.37) * mm, "end": v(7.67, -10.32) * mm});
            skLineSegment(sketch, "E318", {"start": v(7.67, -10.32) * mm, "end": v(7.47, -10.26) * mm});
            skLineSegment(sketch, "E319", {"start": v(7.47, -10.26) * mm, "end": v(7.27, -10.17) * mm});
            skLineSegment(sketch, "E320", {"start": v(7.27, -10.17) * mm, "end": v(7.09, -10.06) * mm});
            skLineSegment(sketch, "E321", {"start": v(7.09, -10.06) * mm, "end": v(6.91, -9.93) * mm});
            skLineSegment(sketch, "E322", {"start": v(6.91, -9.93) * mm, "end": v(6.75, -9.79) * mm});
            skLineSegment(sketch, "E323", {"start": v(6.75, -9.79) * mm, "end": v(6.6, -9.63) * mm});
            skLineSegment(sketch, "E324", {"start": v(6.6, -9.63) * mm, "end": v(6.47, -9.45) * mm});
            skLineSegment(sketch, "E325", {"start": v(6.47, -9.45) * mm, "end": v(6.36, -9.26) * mm});
            skLineSegment(sketch, "E326", {"start": v(6.36, -9.26) * mm, "end": v(6.27, -9.06) * mm});
            skLineSegment(sketch, "E327", {"start": v(6.27, -9.06) * mm, "end": v(6.2, -8.85) * mm});
            skLineSegment(sketch, "E328", {"start": v(6.2, -8.85) * mm, "end": v(6.15, -8.63) * mm});
            skLineSegment(sketch, "E329", {"start": v(6.15, -8.63) * mm, "end": v(6.11, -8.38) * mm});
            skLineSegment(sketch, "E330", {"start": v(6.11, -8.38) * mm, "end": v(6.1, -8.12) * mm});
            skLineSegment(sketch, "E331", {"start": v(6.1, -8.12) * mm, "end": v(6.13, -7.86) * mm});
            skLineSegment(sketch, "E332", {"start": v(6.13, -7.86) * mm, "end": v(6.17, -7.6) * mm});
            skLineSegment(sketch, "E333", {"start": v(6.17, -7.6) * mm, "end": v(6.25, -7.33) * mm});
            skLineSegment(sketch, "E334", {"start": v(6.25, -7.33) * mm, "end": v(6.34, -7.07) * mm});
            skLineSegment(sketch, "E335", {"start": v(6.34, -7.07) * mm, "end": v(6.47, -6.81) * mm});
            skLineSegment(sketch, "E336", {"start": v(6.47, -6.81) * mm, "end": v(6.62, -6.57) * mm});
            skLineSegment(sketch, "E337", {"start": v(6.62, -6.57) * mm, "end": v(6.8, -6.31) * mm});
            skLineSegment(sketch, "E338", {"start": v(6.8, -6.31) * mm, "end": v(7.02, -6.07) * mm});
            skLineSegment(sketch, "E339", {"start": v(7.02, -6.07) * mm, "end": v(7.26, -5.86) * mm});
            skLineSegment(sketch, "E340", {"start": v(7.26, -5.86) * mm, "end": v(7.52, -5.67) * mm});
            skLineSegment(sketch, "E341", {"start": v(7.52, -5.67) * mm, "end": v(7.8, -5.5) * mm});
            skLineSegment(sketch, "E342", {"start": v(7.8, -5.5) * mm, "end": v(8.08, -5.37) * mm});
            skLineSegment(sketch, "E343", {"start": v(8.08, -5.37) * mm, "end": v(8.37, -5.27) * mm});
            skLineSegment(sketch, "E344", {"start": v(8.37, -5.27) * mm, "end": v(8.67, -5.21) * mm});
            skLineSegment(sketch, "E345", {"start": v(15.38, -25.27) * mm, "end": v(16.03, -25.24) * mm});
            skLineSegment(sketch, "E346", {"start": v(16.03, -25.24) * mm, "end": v(16.66, -25.31) * mm});
            skLineSegment(sketch, "E347", {"start": v(16.66, -25.31) * mm, "end": v(17.25, -25.47) * mm});
            skLineSegment(sketch, "E348", {"start": v(17.25, -25.47) * mm, "end": v(17.8, -25.72) * mm});
            skLineSegment(sketch, "E349", {"start": v(17.8, -25.72) * mm, "end": v(18.29, -26.05) * mm});
            skLineSegment(sketch, "E350", {"start": v(18.29, -26.05) * mm, "end": v(18.72, -26.44) * mm});
            skLineSegment(sketch, "E351", {"start": v(18.72, -26.44) * mm, "end": v(19.08, -26.9) * mm});
            skLineSegment(sketch, "E352", {"start": v(19.08, -26.9) * mm, "end": v(19.36, -27.42) * mm});
            skLineSegment(sketch, "E353", {"start": v(19.36, -27.42) * mm, "end": v(19.48, -27.71) * mm});
            skLineSegment(sketch, "E354", {"start": v(19.48, -27.71) * mm, "end": v(19.57, -28.03) * mm});
            skLineSegment(sketch, "E355", {"start": v(19.57, -28.03) * mm, "end": v(19.64, -28.35) * mm});
            skLineSegment(sketch, "E356", {"start": v(19.64, -28.35) * mm, "end": v(19.68, -28.68) * mm});
            skLineSegment(sketch, "E357", {"start": v(19.68, -28.68) * mm, "end": v(19.69, -29.02) * mm});
            skLineSegment(sketch, "E358", {"start": v(19.69, -29.02) * mm, "end": v(19.67, -29.36) * mm});
            skLineSegment(sketch, "E359", {"start": v(19.67, -29.36) * mm, "end": v(19.62, -29.7) * mm});
            skLineSegment(sketch, "E360", {"start": v(19.62, -29.7) * mm, "end": v(19.53, -30.06) * mm});
            skLineSegment(sketch, "E361", {"start": v(19.53, -30.06) * mm, "end": v(19.43, -30.35) * mm});
            skLineSegment(sketch, "E362", {"start": v(19.43, -30.35) * mm, "end": v(19.31, -30.64) * mm});
            skLineSegment(sketch, "E363", {"start": v(19.31, -30.64) * mm, "end": v(19.17, -30.92) * mm});
            skLineSegment(sketch, "E364", {"start": v(19.17, -30.92) * mm, "end": v(19, -31.2) * mm});
            skLineSegment(sketch, "E365", {"start": v(19, -31.2) * mm, "end": v(18.82, -31.46) * mm});
            skLineSegment(sketch, "E366", {"start": v(18.82, -31.46) * mm, "end": v(18.6, -31.71) * mm});
            skLineSegment(sketch, "E367", {"start": v(18.6, -31.71) * mm, "end": v(18.38, -31.95) * mm});
            skLineSegment(sketch, "E368", {"start": v(18.38, -31.95) * mm, "end": v(18.14, -32.17) * mm});
            skLineSegment(sketch, "E369", {"start": v(18.14, -32.17) * mm, "end": v(17.83, -32.4) * mm});
            skLineSegment(sketch, "E370", {"start": v(17.83, -32.4) * mm, "end": v(17.5, -32.61) * mm});
            skLineSegment(sketch, "E371", {"start": v(17.5, -32.61) * mm, "end": v(17.16, -32.8) * mm});
            skLineSegment(sketch, "E372", {"start": v(17.16, -32.8) * mm, "end": v(16.8, -32.94) * mm});
            skLineSegment(sketch, "E373", {"start": v(16.8, -32.94) * mm, "end": v(16.45, -33.05) * mm});
            skLineSegment(sketch, "E374", {"start": v(16.45, -33.05) * mm, "end": v(16.09, -33.14) * mm});
            skLineSegment(sketch, "E375", {"start": v(16.09, -33.14) * mm, "end": v(15.73, -33.19) * mm});
            skLineSegment(sketch, "E376", {"start": v(15.73, -33.19) * mm, "end": v(15.37, -33.2) * mm});
            skLineSegment(sketch, "E377", {"start": v(15.37, -33.2) * mm, "end": v(14.78, -33.17) * mm});
            skLineSegment(sketch, "E378", {"start": v(14.78, -33.17) * mm, "end": v(14.22, -33.05) * mm});
            skLineSegment(sketch, "E379", {"start": v(14.22, -33.05) * mm, "end": v(13.7, -32.87) * mm});
            skLineSegment(sketch, "E380", {"start": v(13.7, -32.87) * mm, "end": v(13.22, -32.6) * mm});
            skLineSegment(sketch, "E381", {"start": v(13.22, -32.6) * mm, "end": v(12.78, -32.28) * mm});
            skLineSegment(sketch, "E382", {"start": v(12.78, -32.28) * mm, "end": v(12.4, -31.9) * mm});
            skLineSegment(sketch, "E383", {"start": v(12.4, -31.9) * mm, "end": v(12.08, -31.47) * mm});
            skLineSegment(sketch, "E384", {"start": v(12.08, -31.47) * mm, "end": v(11.83, -31) * mm});
            skLineSegment(sketch, "E385", {"start": v(11.83, -31) * mm, "end": v(11.73, -30.73) * mm});
            skLineSegment(sketch, "E386", {"start": v(11.73, -30.73) * mm, "end": v(11.64, -30.45) * mm});
            skLineSegment(sketch, "E387", {"start": v(11.64, -30.45) * mm, "end": v(11.58, -30.17) * mm});
            skLineSegment(sketch, "E388", {"start": v(11.58, -30.17) * mm, "end": v(11.54, -29.88) * mm});
            skLineSegment(sketch, "E389", {"start": v(11.54, -29.88) * mm, "end": v(11.52, -29.59) * mm});
            skLineSegment(sketch, "E390", {"start": v(11.52, -29.59) * mm, "end": v(11.52, -29.29) * mm});
            skLineSegment(sketch, "E391", {"start": v(11.52, -29.29) * mm, "end": v(11.55, -28.98) * mm});
            skLineSegment(sketch, "E392", {"start": v(11.55, -28.98) * mm, "end": v(11.6, -28.68) * mm});
            skLineSegment(sketch, "E393", {"start": v(11.6, -28.68) * mm, "end": v(11.68, -28.4) * mm});
            skLineSegment(sketch, "E394", {"start": v(11.68, -28.4) * mm, "end": v(11.76, -28.12) * mm});
            skLineSegment(sketch, "E395", {"start": v(11.76, -28.12) * mm, "end": v(11.88, -27.85) * mm});
            skLineSegment(sketch, "E396", {"start": v(11.88, -27.85) * mm, "end": v(12, -27.58) * mm});
            skLineSegment(sketch, "E397", {"start": v(12, -27.58) * mm, "end": v(12.16, -27.32) * mm});
            skLineSegment(sketch, "E398", {"start": v(12.16, -27.32) * mm, "end": v(12.33, -27.06) * mm});
            skLineSegment(sketch, "E399", {"start": v(12.33, -27.06) * mm, "end": v(12.52, -26.82) * mm});
            skLineSegment(sketch, "E400", {"start": v(12.52, -26.82) * mm, "end": v(12.73, -26.6) * mm});
            skLineSegment(sketch, "E401", {"start": v(12.73, -26.6) * mm, "end": v(13, -26.32) * mm});
            skLineSegment(sketch, "E402", {"start": v(13, -26.32) * mm, "end": v(13.31, -26.08) * mm});
            skLineSegment(sketch, "E403", {"start": v(13.31, -26.08) * mm, "end": v(13.63, -25.87) * mm});
            skLineSegment(sketch, "E404", {"start": v(13.63, -25.87) * mm, "end": v(13.97, -25.69) * mm});
            skLineSegment(sketch, "E405", {"start": v(13.97, -25.69) * mm, "end": v(14.31, -25.54) * mm});
            skLineSegment(sketch, "E406", {"start": v(14.31, -25.54) * mm, "end": v(14.67, -25.41) * mm});
            skLineSegment(sketch, "E407", {"start": v(14.67, -25.41) * mm, "end": v(15.02, -25.32) * mm});
            skLineSegment(sketch, "E408", {"start": v(15.02, -25.32) * mm, "end": v(15.38, -25.27) * mm});
            skLineSegment(sketch, "E409", {"start": v(0.06, -28.7) * mm, "end": v(0.32, -28.69) * mm});
            skLineSegment(sketch, "E410", {"start": v(0.32, -28.69) * mm, "end": v(0.58, -28.7) * mm});
            skLineSegment(sketch, "E411", {"start": v(0.58, -28.7) * mm, "end": v(0.83, -28.73) * mm});
            skLineSegment(sketch, "E412", {"start": v(0.83, -28.73) * mm, "end": v(1.06, -28.79) * mm});
            skLineSegment(sketch, "E413", {"start": v(1.06, -28.79) * mm, "end": v(1.3, -28.87) * mm});
            skLineSegment(sketch, "E414", {"start": v(1.3, -28.87) * mm, "end": v(1.5, -28.98) * mm});
            skLineSegment(sketch, "E415", {"start": v(1.5, -28.98) * mm, "end": v(1.7, -29.1) * mm});
            skLineSegment(sketch, "E416", {"start": v(1.7, -29.1) * mm, "end": v(1.88, -29.25) * mm});
            skLineSegment(sketch, "E417", {"start": v(1.88, -29.25) * mm, "end": v(2.13, -29.52) * mm});
            skLineSegment(sketch, "E418", {"start": v(2.13, -29.52) * mm, "end": v(2.33, -29.83) * mm});
            skLineSegment(sketch, "E419", {"start": v(2.33, -29.83) * mm, "end": v(2.47, -30.18) * mm});
            skLineSegment(sketch, "E420", {"start": v(2.47, -30.18) * mm, "end": v(2.56, -30.56) * mm});
            skLineSegment(sketch, "E421", {"start": v(2.56, -30.56) * mm, "end": v(2.58, -30.95) * mm});
            skLineSegment(sketch, "E422", {"start": v(2.58, -30.95) * mm, "end": v(2.55, -31.36) * mm});
            skLineSegment(sketch, "E423", {"start": v(2.55, -31.36) * mm, "end": v(2.45, -31.77) * mm});
            skLineSegment(sketch, "E424", {"start": v(2.45, -31.77) * mm, "end": v(2.29, -32.17) * mm});
            skLineSegment(sketch, "E425", {"start": v(2.29, -32.17) * mm, "end": v(2.15, -32.43) * mm});
            skLineSegment(sketch, "E426", {"start": v(2.15, -32.43) * mm, "end": v(2, -32.67) * mm});
            skLineSegment(sketch, "E427", {"start": v(2, -32.67) * mm, "end": v(1.8, -32.9) * mm});
            skLineSegment(sketch, "E428", {"start": v(1.8, -32.9) * mm, "end": v(1.6, -33.13) * mm});
            skLineSegment(sketch, "E429", {"start": v(1.6, -33.13) * mm, "end": v(1.38, -33.33) * mm});
            skLineSegment(sketch, "E430", {"start": v(1.38, -33.33) * mm, "end": v(1.14, -33.5) * mm});
            skLineSegment(sketch, "E431", {"start": v(1.14, -33.5) * mm, "end": v(0.9, -33.67) * mm});
            skLineSegment(sketch, "E432", {"start": v(0.9, -33.67) * mm, "end": v(0.63, -33.8) * mm});
            skLineSegment(sketch, "E433", {"start": v(0.63, -33.8) * mm, "end": v(0.36, -33.9) * mm});
            skLineSegment(sketch, "E434", {"start": v(0.36, -33.9) * mm, "end": v(0.1, -33.99) * mm});
            skLineSegment(sketch, "E435", {"start": v(0.1, -33.99) * mm, "end": v(-0.18, -34.04) * mm});
            skLineSegment(sketch, "E436", {"start": v(-0.18, -34.04) * mm, "end": v(-0.45, -34.07) * mm});
            skLineSegment(sketch, "E437", {"start": v(-0.45, -34.07) * mm, "end": v(-0.71, -34.06) * mm});
            skLineSegment(sketch, "E438", {"start": v(-0.71, -34.06) * mm, "end": v(-0.97, -34.03) * mm});
            skLineSegment(sketch, "E439", {"start": v(-0.97, -34.03) * mm, "end": v(-1.22, -33.98) * mm});
            skLineSegment(sketch, "E440", {"start": v(-1.22, -33.98) * mm, "end": v(-1.45, -33.9) * mm});
            skLineSegment(sketch, "E441", {"start": v(-1.45, -33.9) * mm, "end": v(-1.69, -33.78) * mm});
            skLineSegment(sketch, "E442", {"start": v(-1.69, -33.78) * mm, "end": v(-1.9, -33.64) * mm});
            skLineSegment(sketch, "E443", {"start": v(-1.9, -33.64) * mm, "end": v(-2.1, -33.48) * mm});
            skLineSegment(sketch, "E444", {"start": v(-2.1, -33.48) * mm, "end": v(-2.27, -33.3) * mm});
            skLineSegment(sketch, "E445", {"start": v(-2.27, -33.3) * mm, "end": v(-2.42, -33.09) * mm});
            skLineSegment(sketch, "E446", {"start": v(-2.42, -33.09) * mm, "end": v(-2.55, -32.86) * mm});
            skLineSegment(sketch, "E447", {"start": v(-2.55, -32.86) * mm, "end": v(-2.64, -32.62) * mm});
            skLineSegment(sketch, "E448", {"start": v(-2.64, -32.62) * mm, "end": v(-2.71, -32.37) * mm});
            skLineSegment(sketch, "E449", {"start": v(-2.71, -32.37) * mm, "end": v(-2.75, -32.18) * mm});
            skLineSegment(sketch, "E450", {"start": v(-2.75, -32.18) * mm, "end": v(-2.77, -31.98) * mm});
            skLineSegment(sketch, "E451", {"start": v(-2.77, -31.98) * mm, "end": v(-2.77, -31.78) * mm});
            skLineSegment(sketch, "E452", {"start": v(-2.77, -31.78) * mm, "end": v(-2.75, -31.57) * mm});
            skLineSegment(sketch, "E453", {"start": v(-2.75, -31.57) * mm, "end": v(-2.72, -31.37) * mm});
            skLineSegment(sketch, "E454", {"start": v(-2.72, -31.37) * mm, "end": v(-2.68, -31.16) * mm});
            skLineSegment(sketch, "E455", {"start": v(-2.68, -31.16) * mm, "end": v(-2.62, -30.96) * mm});
            skLineSegment(sketch, "E456", {"start": v(-2.62, -30.96) * mm, "end": v(-2.55, -30.76) * mm});
            skLineSegment(sketch, "E457", {"start": v(-2.55, -30.76) * mm, "end": v(-2.45, -30.53) * mm});
            skLineSegment(sketch, "E458", {"start": v(-2.45, -30.53) * mm, "end": v(-2.32, -30.3) * mm});
            skLineSegment(sketch, "E459", {"start": v(-2.32, -30.3) * mm, "end": v(-2.18, -30.1) * mm});
            skLineSegment(sketch, "E460", {"start": v(-2.18, -30.1) * mm, "end": v(-2.03, -29.89) * mm});
            skLineSegment(sketch, "E461", {"start": v(-2.03, -29.89) * mm, "end": v(-1.86, -29.7) * mm});
            skLineSegment(sketch, "E462", {"start": v(-1.86, -29.7) * mm, "end": v(-1.67, -29.52) * mm});
            skLineSegment(sketch, "E463", {"start": v(-1.67, -29.52) * mm, "end": v(-1.47, -29.35) * mm});
            skLineSegment(sketch, "E464", {"start": v(-1.47, -29.35) * mm, "end": v(-1.26, -29.2) * mm});
            skLineSegment(sketch, "E465", {"start": v(-1.26, -29.2) * mm, "end": v(-1.1, -29.1) * mm});
            skLineSegment(sketch, "E466", {"start": v(-1.1, -29.1) * mm, "end": v(-0.95, -29.02) * mm});
            skLineSegment(sketch, "E467", {"start": v(-0.95, -29.02) * mm, "end": v(-0.78, -28.94) * mm});
            skLineSegment(sketch, "E468", {"start": v(-0.78, -28.94) * mm, "end": v(-0.62, -28.87) * mm});
            skLineSegment(sketch, "E469", {"start": v(-0.62, -28.87) * mm, "end": v(-0.45, -28.82) * mm});
            skLineSegment(sketch, "E470", {"start": v(-0.45, -28.82) * mm, "end": v(-0.28, -28.77) * mm});
            skLineSegment(sketch, "E471", {"start": v(-0.28, -28.77) * mm, "end": v(-0.1, -28.73) * mm});
            skLineSegment(sketch, "E472", {"start": v(-0.1, -28.73) * mm, "end": v(0.06, -28.7) * mm});
            skLineSegment(sketch, "E473", {"start": v(6.16, -30.48) * mm, "end": v(6.6, -30.44) * mm});
            skLineSegment(sketch, "E474", {"start": v(6.6, -30.44) * mm, "end": v(7.03, -30.45) * mm});
            skLineSegment(sketch, "E475", {"start": v(7.03, -30.45) * mm, "end": v(7.44, -30.52) * mm});
            skLineSegment(sketch, "E476", {"start": v(7.44, -30.52) * mm, "end": v(7.83, -30.64) * mm});
            skLineSegment(sketch, "E477", {"start": v(7.83, -30.64) * mm, "end": v(8.2, -30.81) * mm});
            skLineSegment(sketch, "E478", {"start": v(8.2, -30.81) * mm, "end": v(8.53, -31.03) * mm});
            skLineSegment(sketch, "E479", {"start": v(8.53, -31.03) * mm, "end": v(8.83, -31.28) * mm});
            skLineSegment(sketch, "E480", {"start": v(8.83, -31.28) * mm, "end": v(9.1, -31.56) * mm});
            skLineSegment(sketch, "E481", {"start": v(9.1, -31.56) * mm, "end": v(9.33, -31.9) * mm});
            skLineSegment(sketch, "E482", {"start": v(9.33, -31.9) * mm, "end": v(9.54, -32.27) * mm});
            skLineSegment(sketch, "E483", {"start": v(9.54, -32.27) * mm, "end": v(9.69, -32.66) * mm});
            skLineSegment(sketch, "E484", {"start": v(9.69, -32.66) * mm, "end": v(9.8, -33.08) * mm});
            skLineSegment(sketch, "E485", {"start": v(9.8, -33.08) * mm, "end": v(9.85, -33.52) * mm});
            skLineSegment(sketch, "E486", {"start": v(9.85, -33.52) * mm, "end": v(9.85, -33.97) * mm});
            skLineSegment(sketch, "E487", {"start": v(9.85, -33.97) * mm, "end": v(9.79, -34.42) * mm});
            skLineSegment(sketch, "E488", {"start": v(9.79, -34.42) * mm, "end": v(9.67, -34.88) * mm});
            skLineSegment(sketch, "E489", {"start": v(9.67, -34.88) * mm, "end": v(9.58, -35.13) * mm});
            skLineSegment(sketch, "E490", {"start": v(9.58, -35.13) * mm, "end": v(9.46, -35.37) * mm});
            skLineSegment(sketch, "E491", {"start": v(9.46, -35.37) * mm, "end": v(9.33, -35.6) * mm});
            skLineSegment(sketch, "E492", {"start": v(9.33, -35.6) * mm, "end": v(9.18, -35.84) * mm});
            skLineSegment(sketch, "E493", {"start": v(9.18, -35.84) * mm, "end": v(9, -36.05) * mm});
            skLineSegment(sketch, "E494", {"start": v(9, -36.05) * mm, "end": v(8.82, -36.25) * mm});
            skLineSegment(sketch, "E495", {"start": v(8.82, -36.25) * mm, "end": v(8.61, -36.44) * mm});
            skLineSegment(sketch, "E496", {"start": v(8.61, -36.44) * mm, "end": v(8.4, -36.61) * mm});
            skLineSegment(sketch, "E497", {"start": v(8.4, -36.61) * mm, "end": v(8.16, -36.76) * mm});
            skLineSegment(sketch, "E498", {"start": v(8.16, -36.76) * mm, "end": v(7.93, -36.89) * mm});
            skLineSegment(sketch, "E499", {"start": v(7.93, -36.89) * mm, "end": v(7.69, -37) * mm});
            skLineSegment(sketch, "E500", {"start": v(7.69, -37) * mm, "end": v(7.44, -37.08) * mm});
            skLineSegment(sketch, "E501", {"start": v(7.44, -37.08) * mm, "end": v(7.2, -37.14) * mm});
            skLineSegment(sketch, "E502", {"start": v(7.2, -37.14) * mm, "end": v(6.94, -37.18) * mm});
            skLineSegment(sketch, "E503", {"start": v(6.94, -37.18) * mm, "end": v(6.7, -37.2) * mm});
            skLineSegment(sketch, "E504", {"start": v(6.7, -37.2) * mm, "end": v(6.45, -37.2) * mm});
            skLineSegment(sketch, "E505", {"start": v(6.45, -37.2) * mm, "end": v(6.08, -37.16) * mm});
            skLineSegment(sketch, "E506", {"start": v(6.08, -37.16) * mm, "end": v(5.72, -37.08) * mm});
            skLineSegment(sketch, "E507", {"start": v(5.72, -37.08) * mm, "end": v(5.39, -36.96) * mm});
            skLineSegment(sketch, "E508", {"start": v(5.39, -36.96) * mm, "end": v(5.07, -36.81) * mm});
            skLineSegment(sketch, "E509", {"start": v(5.07, -36.81) * mm, "end": v(4.78, -36.62) * mm});
            skLineSegment(sketch, "E510", {"start": v(4.78, -36.62) * mm, "end": v(4.52, -36.4) * mm});
            skLineSegment(sketch, "E511", {"start": v(4.52, -36.4) * mm, "end": v(4.27, -36.16) * mm});
            skLineSegment(sketch, "E512", {"start": v(4.27, -36.16) * mm, "end": v(4.06, -35.9) * mm});
            skLineSegment(sketch, "E513", {"start": v(4.06, -35.9) * mm, "end": v(3.94, -35.7) * mm});
            skLineSegment(sketch, "E514", {"start": v(3.94, -35.7) * mm, "end": v(3.83, -35.51) * mm});
            skLineSegment(sketch, "E515", {"start": v(3.83, -35.51) * mm, "end": v(3.73, -35.31) * mm});
            skLineSegment(sketch, "E516", {"start": v(3.73, -35.31) * mm, "end": v(3.65, -35.1) * mm});
            skLineSegment(sketch, "E517", {"start": v(3.65, -35.1) * mm, "end": v(3.57, -34.89) * mm});
            skLineSegment(sketch, "E518", {"start": v(3.57, -34.89) * mm, "end": v(3.52, -34.66) * mm});
            skLineSegment(sketch, "E519", {"start": v(3.52, -34.66) * mm, "end": v(3.47, -34.43) * mm});
            skLineSegment(sketch, "E520", {"start": v(3.47, -34.43) * mm, "end": v(3.45, -34.2) * mm});
            skLineSegment(sketch, "E521", {"start": v(3.45, -34.2) * mm, "end": v(3.43, -33.9) * mm});
            skLineSegment(sketch, "E522", {"start": v(3.43, -33.9) * mm, "end": v(3.45, -33.58) * mm});
            skLineSegment(sketch, "E523", {"start": v(3.45, -33.58) * mm, "end": v(3.5, -33.26) * mm});
            skLineSegment(sketch, "E524", {"start": v(3.5, -33.26) * mm, "end": v(3.56, -32.94) * mm});
            skLineSegment(sketch, "E525", {"start": v(3.56, -32.94) * mm, "end": v(3.67, -32.63) * mm});
            skLineSegment(sketch, "E526", {"start": v(3.67, -32.63) * mm, "end": v(3.8, -32.32) * mm});
            skLineSegment(sketch, "E527", {"start": v(3.8, -32.32) * mm, "end": v(3.97, -32.02) * mm});
            skLineSegment(sketch, "E528", {"start": v(3.97, -32.02) * mm, "end": v(4.16, -31.74) * mm});
            skLineSegment(sketch, "E529", {"start": v(4.16, -31.74) * mm, "end": v(4.36, -31.5) * mm});
            skLineSegment(sketch, "E530", {"start": v(4.36, -31.5) * mm, "end": v(4.57, -31.29) * mm});
            skLineSegment(sketch, "E531", {"start": v(4.57, -31.29) * mm, "end": v(4.81, -31.1) * mm});
            skLineSegment(sketch, "E532", {"start": v(4.81, -31.1) * mm, "end": v(5.06, -30.92) * mm});
            skLineSegment(sketch, "E533", {"start": v(5.06, -30.92) * mm, "end": v(5.32, -30.77) * mm});
            skLineSegment(sketch, "E534", {"start": v(5.32, -30.77) * mm, "end": v(5.6, -30.65) * mm});
            skLineSegment(sketch, "E535", {"start": v(5.6, -30.65) * mm, "end": v(5.88, -30.55) * mm});
            skLineSegment(sketch, "E536", {"start": v(5.88, -30.55) * mm, "end": v(6.16, -30.48) * mm});
            skLineSegment(sketch, "E537", {"start": v(12.87, -13.06) * mm, "end": v(13.23, -13.06) * mm});
            skLineSegment(sketch, "E538", {"start": v(13.23, -13.06) * mm, "end": v(13.6, -13.06) * mm});
            skLineSegment(sketch, "E539", {"start": v(13.6, -13.06) * mm, "end": v(13.96, -13.06) * mm});
            skLineSegment(sketch, "E540", {"start": v(13.96, -13.06) * mm, "end": v(14.32, -13.06) * mm});
            skLineSegment(sketch, "E541", {"start": v(14.32, -13.06) * mm, "end": v(14.68, -13.06) * mm});
            skLineSegment(sketch, "E542", {"start": v(14.68, -13.06) * mm, "end": v(15.04, -13.06) * mm});
            skLineSegment(sketch, "E543", {"start": v(15.04, -13.06) * mm, "end": v(15.4, -13.06) * mm});
            skLineSegment(sketch, "E544", {"start": v(15.4, -13.06) * mm, "end": v(15.76, -13.06) * mm});
            skLineSegment(sketch, "E545", {"start": v(15.76, -13.06) * mm, "end": v(15.87, -13.73) * mm});
            skLineSegment(sketch, "E546", {"start": v(15.87, -13.73) * mm, "end": v(15.97, -14.4) * mm});
            skLineSegment(sketch, "E547", {"start": v(15.97, -14.4) * mm, "end": v(16.07, -15.06) * mm});
            skLineSegment(sketch, "E548", {"start": v(16.07, -15.06) * mm, "end": v(16.17, -15.73) * mm});
            skLineSegment(sketch, "E549", {"start": v(16.17, -15.73) * mm, "end": v(16.27, -16.4) * mm});
            skLineSegment(sketch, "E550", {"start": v(16.27, -16.4) * mm, "end": v(16.37, -17.07) * mm});
            skLineSegment(sketch, "E551", {"start": v(16.37, -17.07) * mm, "end": v(16.48, -17.73) * mm});
            skLineSegment(sketch, "E552", {"start": v(16.48, -17.73) * mm, "end": v(16.58, -18.4) * mm});
            skLineSegment(sketch, "E553", {"start": v(16.58, -18.4) * mm, "end": v(16.6, -18.4) * mm});
            skLineSegment(sketch, "E554", {"start": v(16.6, -18.4) * mm, "end": v(16.62, -18.4) * mm});
            skLineSegment(sketch, "E555", {"start": v(16.62, -18.4) * mm, "end": v(16.65, -18.4) * mm});
            skLineSegment(sketch, "E556", {"start": v(16.65, -18.4) * mm, "end": v(16.67, -18.4) * mm});
            skLineSegment(sketch, "E557", {"start": v(16.67, -18.4) * mm, "end": v(16.7, -18.4) * mm});
            skLineSegment(sketch, "E558", {"start": v(16.7, -18.4) * mm, "end": v(16.73, -18.4) * mm});
            skLineSegment(sketch, "E559", {"start": v(16.73, -18.4) * mm, "end": v(16.75, -18.4) * mm});
            skLineSegment(sketch, "E560", {"start": v(16.75, -18.4) * mm, "end": v(16.76, -18.4) * mm});
            skLineSegment(sketch, "E561", {"start": v(16.76, -18.4) * mm, "end": v(16.87, -17.86) * mm});
            skLineSegment(sketch, "E562", {"start": v(16.87, -17.86) * mm, "end": v(17, -17.2) * mm});
            skLineSegment(sketch, "E563", {"start": v(17, -17.2) * mm, "end": v(17.15, -16.49) * mm});
            skLineSegment(sketch, "E564", {"start": v(17.15, -16.49) * mm, "end": v(17.3, -15.73) * mm});
            skLineSegment(sketch, "E565", {"start": v(17.3, -15.73) * mm, "end": v(17.46, -14.97) * mm});
            skLineSegment(sketch, "E566", {"start": v(17.46, -14.97) * mm, "end": v(17.61, -14.25) * mm});
            skLineSegment(sketch, "E567", {"start": v(17.61, -14.25) * mm, "end": v(17.74, -13.6) * mm});
            skLineSegment(sketch, "E568", {"start": v(17.74, -13.6) * mm, "end": v(17.85, -13.06) * mm});
            skLineSegment(sketch, "E569", {"start": v(17.85, -13.06) * mm, "end": v(18.2, -13.06) * mm});
            skLineSegment(sketch, "E570", {"start": v(18.2, -13.06) * mm, "end": v(18.56, -13.06) * mm});
            skLineSegment(sketch, "E571", {"start": v(18.56, -13.06) * mm, "end": v(18.91, -13.06) * mm});
            skLineSegment(sketch, "E572", {"start": v(18.91, -13.06) * mm, "end": v(19.27, -13.06) * mm});
            skLineSegment(sketch, "E573", {"start": v(19.27, -13.06) * mm, "end": v(19.62, -13.06) * mm});
            skLineSegment(sketch, "E574", {"start": v(19.62, -13.06) * mm, "end": v(19.98, -13.06) * mm});
            skLineSegment(sketch, "E575", {"start": v(19.98, -13.06) * mm, "end": v(20.33, -13.06) * mm});
            skLineSegment(sketch, "E576", {"start": v(20.33, -13.06) * mm, "end": v(20.68, -13.06) * mm});
            skLineSegment(sketch, "E577", {"start": v(20.68, -13.06) * mm, "end": v(20.53, -13.8) * mm});
            skLineSegment(sketch, "E578", {"start": v(20.53, -13.8) * mm, "end": v(20.25, -15.18) * mm});
            skLineSegment(sketch, "E579", {"start": v(20.25, -15.18) * mm, "end": v(19.89, -17) * mm});
            skLineSegment(sketch, "E580", {"start": v(19.89, -17) * mm, "end": v(19.47, -19.02) * mm});
            skLineSegment(sketch, "E581", {"start": v(19.47, -19.02) * mm, "end": v(19.06, -21.03) * mm});
            skLineSegment(sketch, "E582", {"start": v(19.06, -21.03) * mm, "end": v(18.7, -22.82) * mm});
            skLineSegment(sketch, "E583", {"start": v(18.7, -22.82) * mm, "end": v(18.42, -24.17) * mm});
            skLineSegment(sketch, "E584", {"start": v(18.42, -24.17) * mm, "end": v(18.28, -24.86) * mm});
            skLineSegment(sketch, "E585", {"start": v(18.28, -24.86) * mm, "end": v(17.9, -24.86) * mm});
            skLineSegment(sketch, "E586", {"start": v(17.9, -24.86) * mm, "end": v(17.52, -24.86) * mm});
            skLineSegment(sketch, "E587", {"start": v(17.52, -24.86) * mm, "end": v(17.15, -24.86) * mm});
            skLineSegment(sketch, "E588", {"start": v(17.15, -24.86) * mm, "end": v(16.77, -24.86) * mm});
            skLineSegment(sketch, "E589", {"start": v(16.77, -24.86) * mm, "end": v(16.4, -24.86) * mm});
            skLineSegment(sketch, "E590", {"start": v(16.4, -24.86) * mm, "end": v(16.02, -24.86) * mm});
            skLineSegment(sketch, "E591", {"start": v(16.02, -24.86) * mm, "end": v(15.64, -24.86) * mm});
            skLineSegment(sketch, "E592", {"start": v(15.64, -24.86) * mm, "end": v(15.27, -24.86) * mm});
            skLineSegment(sketch, "E593", {"start": v(15.27, -24.86) * mm, "end": v(15.2, -24.5) * mm});
            skLineSegment(sketch, "E594", {"start": v(15.2, -24.5) * mm, "end": v(15.13, -23.91) * mm});
            skLineSegment(sketch, "E595", {"start": v(15.13, -23.91) * mm, "end": v(15.02, -23.18) * mm});
            skLineSegment(sketch, "E596", {"start": v(15.02, -23.18) * mm, "end": v(14.91, -22.37) * mm});
            skLineSegment(sketch, "E597", {"start": v(14.91, -22.37) * mm, "end": v(14.8, -21.52) * mm});
            skLineSegment(sketch, "E598", {"start": v(14.8, -21.52) * mm, "end": v(14.69, -20.72) * mm});
            skLineSegment(sketch, "E599", {"start": v(14.69, -20.72) * mm, "end": v(14.6, -20.02) * mm});
            skLineSegment(sketch, "E600", {"start": v(14.6, -20.02) * mm, "end": v(14.52, -19.48) * mm});
            skLineSegment(sketch, "E601", {"start": v(14.52, -19.48) * mm, "end": v(14.5, -19.49) * mm});
            skLineSegment(sketch, "E602", {"start": v(14.5, -19.49) * mm, "end": v(14.5, -19.49) * mm});
            skLineSegment(sketch, "E603", {"start": v(14.5, -19.49) * mm, "end": v(14.48, -19.49) * mm});
            skLineSegment(sketch, "E604", {"start": v(14.48, -19.49) * mm, "end": v(14.46, -19.5) * mm});
            skLineSegment(sketch, "E605", {"start": v(14.46, -19.5) * mm, "end": v(14.45, -19.5) * mm});
            skLineSegment(sketch, "E606", {"start": v(14.45, -19.5) * mm, "end": v(14.43, -19.5) * mm});
            skLineSegment(sketch, "E607", {"start": v(14.43, -19.5) * mm, "end": v(14.42, -19.5) * mm});
            skLineSegment(sketch, "E608", {"start": v(14.42, -19.5) * mm, "end": v(14.4, -19.5) * mm});
            skLineSegment(sketch, "E609", {"start": v(14.4, -19.5) * mm, "end": v(14.27, -20.17) * mm});
            skLineSegment(sketch, "E610", {"start": v(14.27, -20.17) * mm, "end": v(14.13, -20.84) * mm});
            skLineSegment(sketch, "E611", {"start": v(14.13, -20.84) * mm, "end": v(14, -21.51) * mm});
            skLineSegment(sketch, "E612", {"start": v(14, -21.51) * mm, "end": v(13.86, -22.18) * mm});
            skLineSegment(sketch, "E613", {"start": v(13.86, -22.18) * mm, "end": v(13.72, -22.85) * mm});
            skLineSegment(sketch, "E614", {"start": v(13.72, -22.85) * mm, "end": v(13.58, -23.52) * mm});
            skLineSegment(sketch, "E615", {"start": v(13.58, -23.52) * mm, "end": v(13.45, -24.2) * mm});
            skLineSegment(sketch, "E616", {"start": v(13.45, -24.2) * mm, "end": v(13.3, -24.86) * mm});
            skLineSegment(sketch, "E617", {"start": v(13.3, -24.86) * mm, "end": v(12.95, -24.86) * mm});
            skLineSegment(sketch, "E618", {"start": v(12.95, -24.86) * mm, "end": v(12.6, -24.86) * mm});
            skLineSegment(sketch, "E619", {"start": v(12.6, -24.86) * mm, "end": v(12.24, -24.86) * mm});
            skLineSegment(sketch, "E620", {"start": v(12.24, -24.86) * mm, "end": v(11.89, -24.86) * mm});
            skLineSegment(sketch, "E621", {"start": v(11.89, -24.86) * mm, "end": v(11.53, -24.86) * mm});
            skLineSegment(sketch, "E622", {"start": v(11.53, -24.86) * mm, "end": v(11.18, -24.86) * mm});
            skLineSegment(sketch, "E623", {"start": v(11.18, -24.86) * mm, "end": v(10.82, -24.86) * mm});
            skLineSegment(sketch, "E624", {"start": v(10.82, -24.86) * mm, "end": v(10.47, -24.86) * mm});
            skLineSegment(sketch, "E625", {"start": v(10.47, -24.86) * mm, "end": v(10.77, -23.39) * mm});
            skLineSegment(sketch, "E626", {"start": v(10.77, -23.39) * mm, "end": v(11.07, -21.91) * mm});
            skLineSegment(sketch, "E627", {"start": v(11.07, -21.91) * mm, "end": v(11.37, -20.44) * mm});
            skLineSegment(sketch, "E628", {"start": v(11.37, -20.44) * mm, "end": v(11.67, -18.96) * mm});
            skLineSegment(sketch, "E629", {"start": v(11.67, -18.96) * mm, "end": v(11.97, -17.49) * mm});
            skLineSegment(sketch, "E630", {"start": v(11.97, -17.49) * mm, "end": v(12.27, -16.01) * mm});
            skLineSegment(sketch, "E631", {"start": v(12.27, -16.01) * mm, "end": v(12.57, -14.54) * mm});
            skLineSegment(sketch, "E632", {"start": v(12.57, -14.54) * mm, "end": v(12.87, -13.06) * mm});
            skLineSegment(sketch, "E633", {"start": v(-6.02, -13.92) * mm, "end": v(-5.73, -13.92) * mm});
            skLineSegment(sketch, "E634", {"start": v(-5.73, -13.92) * mm, "end": v(-5.45, -13.92) * mm});
            skLineSegment(sketch, "E635", {"start": v(-5.45, -13.92) * mm, "end": v(-5.16, -13.92) * mm});
            skLineSegment(sketch, "E636", {"start": v(-5.16, -13.92) * mm, "end": v(-4.87, -13.92) * mm});
            skLineSegment(sketch, "E637", {"start": v(-4.87, -13.92) * mm, "end": v(-4.58, -13.92) * mm});
            skLineSegment(sketch, "E638", {"start": v(-4.58, -13.92) * mm, "end": v(-4.3, -13.92) * mm});
            skLineSegment(sketch, "E639", {"start": v(-4.3, -13.92) * mm, "end": v(-4, -13.92) * mm});
            skLineSegment(sketch, "E640", {"start": v(-4, -13.92) * mm, "end": v(-3.71, -13.92) * mm});
            skLineSegment(sketch, "E641", {"start": v(-3.71, -13.92) * mm, "end": v(-4.1, -14.7) * mm});
            skLineSegment(sketch, "E642", {"start": v(-4.1, -14.7) * mm, "end": v(-4.49, -15.5) * mm});
            skLineSegment(sketch, "E643", {"start": v(-4.49, -15.5) * mm, "end": v(-4.88, -16.29) * mm});
            skLineSegment(sketch, "E644", {"start": v(-4.88, -16.29) * mm, "end": v(-5.28, -17.09) * mm});
            skLineSegment(sketch, "E645", {"start": v(-5.28, -17.09) * mm, "end": v(-5.67, -17.89) * mm});
            skLineSegment(sketch, "E646", {"start": v(-5.67, -17.89) * mm, "end": v(-6.07, -18.68) * mm});
            skLineSegment(sketch, "E647", {"start": v(-6.07, -18.68) * mm, "end": v(-6.46, -19.47) * mm});
            skLineSegment(sketch, "E648", {"start": v(-6.46, -19.47) * mm, "end": v(-6.85, -20.25) * mm});
            skLineSegment(sketch, "E649", {"start": v(-6.85, -20.25) * mm, "end": v(-6.92, -20.43) * mm});
            skLineSegment(sketch, "E650", {"start": v(-6.92, -20.43) * mm, "end": v(-7, -20.78) * mm});
            skLineSegment(sketch, "E651", {"start": v(-7, -20.78) * mm, "end": v(-7.12, -21.26) * mm});
            skLineSegment(sketch, "E652", {"start": v(-7.12, -21.26) * mm, "end": v(-7.24, -21.82) * mm});
            skLineSegment(sketch, "E653", {"start": v(-7.24, -21.82) * mm, "end": v(-7.36, -22.42) * mm});
            skLineSegment(sketch, "E654", {"start": v(-7.36, -22.42) * mm, "end": v(-7.48, -23.01) * mm});
            skLineSegment(sketch, "E655", {"start": v(-7.48, -23.01) * mm, "end": v(-7.6, -23.56) * mm});
            skLineSegment(sketch, "E656", {"start": v(-7.6, -23.56) * mm, "end": v(-7.68, -24.01) * mm});
            skLineSegment(sketch, "E657", {"start": v(-7.68, -24.01) * mm, "end": v(-7.98, -24.01) * mm});
            skLineSegment(sketch, "E658", {"start": v(-7.98, -24.01) * mm, "end": v(-8.27, -24.01) * mm});
            skLineSegment(sketch, "E659", {"start": v(-8.27, -24.01) * mm, "end": v(-8.56, -24.01) * mm});
            skLineSegment(sketch, "E660", {"start": v(-8.56, -24.01) * mm, "end": v(-8.85, -24.01) * mm});
            skLineSegment(sketch, "E661", {"start": v(-8.85, -24.01) * mm, "end": v(-9.14, -24.01) * mm});
            skLineSegment(sketch, "E662", {"start": v(-9.14, -24.01) * mm, "end": v(-9.43, -24.01) * mm});
            skLineSegment(sketch, "E663", {"start": v(-9.43, -24.01) * mm, "end": v(-9.73, -24.01) * mm});
            skLineSegment(sketch, "E664", {"start": v(-9.73, -24.01) * mm, "end": v(-10.02, -24.02) * mm});
            skLineSegment(sketch, "E665", {"start": v(-10.02, -24.02) * mm, "end": v(-9.93, -23.56) * mm});
            skLineSegment(sketch, "E666", {"start": v(-9.93, -23.56) * mm, "end": v(-9.82, -23) * mm});
            skLineSegment(sketch, "E667", {"start": v(-9.82, -23) * mm, "end": v(-9.7, -22.41) * mm});
            skLineSegment(sketch, "E668", {"start": v(-9.7, -22.41) * mm, "end": v(-9.58, -21.82) * mm});
            skLineSegment(sketch, "E669", {"start": v(-9.58, -21.82) * mm, "end": v(-9.46, -21.27) * mm});
            skLineSegment(sketch, "E670", {"start": v(-9.46, -21.27) * mm, "end": v(-9.37, -20.8) * mm});
            skLineSegment(sketch, "E671", {"start": v(-9.37, -20.8) * mm, "end": v(-9.3, -20.47) * mm});
            skLineSegment(sketch, "E672", {"start": v(-9.3, -20.47) * mm, "end": v(-9.29, -20.3) * mm});
            skLineSegment(sketch, "E673", {"start": v(-9.29, -20.3) * mm, "end": v(-9.35, -19.5) * mm});
            skLineSegment(sketch, "E674", {"start": v(-9.35, -19.5) * mm, "end": v(-9.42, -18.71) * mm});
            skLineSegment(sketch, "E675", {"start": v(-9.42, -18.71) * mm, "end": v(-9.49, -17.91) * mm});
            skLineSegment(sketch, "E676", {"start": v(-9.49, -17.91) * mm, "end": v(-9.55, -17.12) * mm});
            skLineSegment(sketch, "E677", {"start": v(-9.55, -17.12) * mm, "end": v(-9.62, -16.32) * mm});
            skLineSegment(sketch, "E678", {"start": v(-9.62, -16.32) * mm, "end": v(-9.69, -15.52) * mm});
            skLineSegment(sketch, "E679", {"start": v(-9.69, -15.52) * mm, "end": v(-9.75, -14.72) * mm});
            skLineSegment(sketch, "E680", {"start": v(-9.75, -14.72) * mm, "end": v(-9.82, -13.93) * mm});
            skLineSegment(sketch, "E681", {"start": v(-9.82, -13.93) * mm, "end": v(-9.53, -13.93) * mm});
            skLineSegment(sketch, "E682", {"start": v(-9.53, -13.93) * mm, "end": v(-9.24, -13.93) * mm});
            skLineSegment(sketch, "E683", {"start": v(-9.24, -13.93) * mm, "end": v(-8.95, -13.93) * mm});
            skLineSegment(sketch, "E684", {"start": v(-8.95, -13.93) * mm, "end": v(-8.66, -13.93) * mm});
            skLineSegment(sketch, "E685", {"start": v(-8.66, -13.93) * mm, "end": v(-8.37, -13.92) * mm});
            skLineSegment(sketch, "E686", {"start": v(-8.37, -13.92) * mm, "end": v(-8.08, -13.92) * mm});
            skLineSegment(sketch, "E687", {"start": v(-8.08, -13.92) * mm, "end": v(-7.8, -13.92) * mm});
            skLineSegment(sketch, "E688", {"start": v(-7.8, -13.92) * mm, "end": v(-7.5, -13.92) * mm});
            skLineSegment(sketch, "E689", {"start": v(-7.5, -13.92) * mm, "end": v(-7.52, -14.42) * mm});
            skLineSegment(sketch, "E690", {"start": v(-7.52, -14.42) * mm, "end": v(-7.53, -14.92) * mm});
            skLineSegment(sketch, "E691", {"start": v(-7.53, -14.92) * mm, "end": v(-7.54, -15.41) * mm});
            skLineSegment(sketch, "E692", {"start": v(-7.54, -15.41) * mm, "end": v(-7.56, -15.9) * mm});
            skLineSegment(sketch, "E693", {"start": v(-7.56, -15.9) * mm, "end": v(-7.57, -16.4) * mm});
            skLineSegment(sketch, "E694", {"start": v(-7.57, -16.4) * mm, "end": v(-7.59, -16.9) * mm});
            skLineSegment(sketch, "E695", {"start": v(-7.59, -16.9) * mm, "end": v(-7.61, -17.4) * mm});
            skLineSegment(sketch, "E696", {"start": v(-7.61, -17.4) * mm, "end": v(-7.64, -17.9) * mm});
            skLineSegment(sketch, "E697", {"start": v(-7.64, -17.9) * mm, "end": v(-7.62, -17.9) * mm});
            skLineSegment(sketch, "E698", {"start": v(-7.62, -17.9) * mm, "end": v(-7.6, -17.9) * mm});
            skLineSegment(sketch, "E699", {"start": v(-7.6, -17.9) * mm, "end": v(-7.6, -17.9) * mm});
            skLineSegment(sketch, "E700", {"start": v(-7.6, -17.9) * mm, "end": v(-7.58, -17.9) * mm});
            skLineSegment(sketch, "E701", {"start": v(-7.58, -17.9) * mm, "end": v(-7.56, -17.9) * mm});
            skLineSegment(sketch, "E702", {"start": v(-7.56, -17.9) * mm, "end": v(-7.55, -17.9) * mm});
            skLineSegment(sketch, "E703", {"start": v(-7.55, -17.9) * mm, "end": v(-7.53, -17.9) * mm});
            skLineSegment(sketch, "E704", {"start": v(-7.53, -17.9) * mm, "end": v(-7.52, -17.9) * mm});
            skLineSegment(sketch, "E705", {"start": v(-7.52, -17.9) * mm, "end": v(-7.34, -17.4) * mm});
            skLineSegment(sketch, "E706", {"start": v(-7.34, -17.4) * mm, "end": v(-7.16, -16.9) * mm});
            skLineSegment(sketch, "E707", {"start": v(-7.16, -16.9) * mm, "end": v(-6.98, -16.4) * mm});
            skLineSegment(sketch, "E708", {"start": v(-6.98, -16.4) * mm, "end": v(-6.8, -15.9) * mm});
            skLineSegment(sketch, "E709", {"start": v(-6.8, -15.9) * mm, "end": v(-6.6, -15.41) * mm});
            skLineSegment(sketch, "E710", {"start": v(-6.6, -15.41) * mm, "end": v(-6.42, -14.91) * mm});
            skLineSegment(sketch, "E711", {"start": v(-6.42, -14.91) * mm, "end": v(-6.22, -14.42) * mm});
            skLineSegment(sketch, "E712", {"start": v(-6.22, -14.42) * mm, "end": v(-6.02, -13.92) * mm});
            skLineSegment(sketch, "E713", {"start": v(-13.3, -13.92) * mm, "end": v(-13.05, -13.92) * mm});
            skLineSegment(sketch, "E714", {"start": v(-13.05, -13.92) * mm, "end": v(-12.77, -13.92) * mm});
            skLineSegment(sketch, "E715", {"start": v(-12.77, -13.92) * mm, "end": v(-12.47, -13.92) * mm});
            skLineSegment(sketch, "E716", {"start": v(-12.47, -13.92) * mm, "end": v(-12.16, -13.92) * mm});
            skLineSegment(sketch, "E717", {"start": v(-12.16, -13.92) * mm, "end": v(-11.83, -13.92) * mm});
            skLineSegment(sketch, "E718", {"start": v(-11.83, -13.92) * mm, "end": v(-11.48, -13.92) * mm});
            skLineSegment(sketch, "E719", {"start": v(-11.48, -13.92) * mm, "end": v(-11.13, -13.92) * mm});
            skLineSegment(sketch, "E720", {"start": v(-11.13, -13.92) * mm, "end": v(-10.77, -13.92) * mm});
            skLineSegment(sketch, "E721", {"start": v(-10.77, -13.92) * mm, "end": v(-10.88, -14.44) * mm});
            skLineSegment(sketch, "E722", {"start": v(-10.88, -14.44) * mm, "end": v(-11.05, -15.28) * mm});
            skLineSegment(sketch, "E723", {"start": v(-11.05, -15.28) * mm, "end": v(-11.27, -16.37) * mm});
            skLineSegment(sketch, "E724", {"start": v(-11.27, -16.37) * mm, "end": v(-11.52, -17.6) * mm});
            skLineSegment(sketch, "E725", {"start": v(-11.52, -17.6) * mm, "end": v(-11.78, -18.88) * mm});
            skLineSegment(sketch, "E726", {"start": v(-11.78, -18.88) * mm, "end": v(-12.03, -20.12) * mm});
            skLineSegment(sketch, "E727", {"start": v(-12.03, -20.12) * mm, "end": v(-12.25, -21.22) * mm});
            skLineSegment(sketch, "E728", {"start": v(-12.25, -21.22) * mm, "end": v(-12.43, -22.1) * mm});
            skLineSegment(sketch, "E729", {"start": v(-12.43, -22.1) * mm, "end": v(-12.23, -22.1) * mm});
            skLineSegment(sketch, "E730", {"start": v(-12.23, -22.1) * mm, "end": v(-12.03, -22.1) * mm});
            skLineSegment(sketch, "E731", {"start": v(-12.03, -22.1) * mm, "end": v(-11.83, -22.1) * mm});
            skLineSegment(sketch, "E732", {"start": v(-11.83, -22.1) * mm, "end": v(-11.63, -22.1) * mm});
            skLineSegment(sketch, "E733", {"start": v(-11.63, -22.1) * mm, "end": v(-11.43, -22.1) * mm});
            skLineSegment(sketch, "E734", {"start": v(-11.43, -22.1) * mm, "end": v(-11.22, -22.1) * mm});
            skLineSegment(sketch, "E735", {"start": v(-11.22, -22.1) * mm, "end": v(-11.02, -22.1) * mm});
            skLineSegment(sketch, "E736", {"start": v(-11.02, -22.1) * mm, "end": v(-10.82, -22.1) * mm});
            skLineSegment(sketch, "E737", {"start": v(-10.82, -22.1) * mm, "end": v(-10.87, -22.33) * mm});
            skLineSegment(sketch, "E738", {"start": v(-10.87, -22.33) * mm, "end": v(-10.92, -22.57) * mm});
            skLineSegment(sketch, "E739", {"start": v(-10.92, -22.57) * mm, "end": v(-10.96, -22.8) * mm});
            skLineSegment(sketch, "E740", {"start": v(-10.96, -22.8) * mm, "end": v(-11.01, -23.04) * mm});
            skLineSegment(sketch, "E741", {"start": v(-11.01, -23.04) * mm, "end": v(-11.06, -23.28) * mm});
            skLineSegment(sketch, "E742", {"start": v(-11.06, -23.28) * mm, "end": v(-11.11, -23.52) * mm});
            skLineSegment(sketch, "E743", {"start": v(-11.11, -23.52) * mm, "end": v(-11.16, -23.77) * mm});
            skLineSegment(sketch, "E744", {"start": v(-11.16, -23.77) * mm, "end": v(-11.21, -24.01) * mm});
            skLineSegment(sketch, "E745", {"start": v(-11.21, -24.01) * mm, "end": v(-11.74, -24.01) * mm});
            skLineSegment(sketch, "E746", {"start": v(-11.74, -24.01) * mm, "end": v(-12.27, -24.01) * mm});
            skLineSegment(sketch, "E747", {"start": v(-12.27, -24.01) * mm, "end": v(-12.79, -24.01) * mm});
            skLineSegment(sketch, "E748", {"start": v(-12.79, -24.01) * mm, "end": v(-13.31, -24.01) * mm});
            skLineSegment(sketch, "E749", {"start": v(-13.31, -24.01) * mm, "end": v(-13.83, -24.01) * mm});
            skLineSegment(sketch, "E750", {"start": v(-13.83, -24.01) * mm, "end": v(-14.35, -24.01) * mm});
            skLineSegment(sketch, "E751", {"start": v(-14.35, -24.01) * mm, "end": v(-14.86, -24.01) * mm});
            skLineSegment(sketch, "E752", {"start": v(-14.86, -24.01) * mm, "end": v(-15.36, -24.01) * mm});
            skLineSegment(sketch, "E753", {"start": v(-15.36, -24.01) * mm, "end": v(-15.1, -22.76) * mm});
            skLineSegment(sketch, "E754", {"start": v(-15.1, -22.76) * mm, "end": v(-14.85, -21.5) * mm});
            skLineSegment(sketch, "E755", {"start": v(-14.85, -21.5) * mm, "end": v(-14.59, -20.23) * mm});
            skLineSegment(sketch, "E756", {"start": v(-14.59, -20.23) * mm, "end": v(-14.33, -18.97) * mm});
            skLineSegment(sketch, "E757", {"start": v(-14.33, -18.97) * mm, "end": v(-14.07, -17.7) * mm});
            skLineSegment(sketch, "E758", {"start": v(-14.07, -17.7) * mm, "end": v(-13.8, -16.43) * mm});
            skLineSegment(sketch, "E759", {"start": v(-13.8, -16.43) * mm, "end": v(-13.55, -15.17) * mm});
            skLineSegment(sketch, "E760", {"start": v(-13.55, -15.17) * mm, "end": v(-13.3, -13.92) * mm});
            skLineSegment(sketch, "E761", {"start": v(-17.72, -13.72) * mm, "end": v(-17.45, -13.7) * mm});
            skLineSegment(sketch, "E762", {"start": v(-17.45, -13.7) * mm, "end": v(-17.18, -13.7) * mm});
            skLineSegment(sketch, "E763", {"start": v(-17.18, -13.7) * mm, "end": v(-16.92, -13.73) * mm});
            skLineSegment(sketch, "E764", {"start": v(-16.92, -13.73) * mm, "end": v(-16.67, -13.76) * mm});
            skLineSegment(sketch, "E765", {"start": v(-16.67, -13.76) * mm, "end": v(-16.42, -13.82) * mm});
            skLineSegment(sketch, "E766", {"start": v(-16.42, -13.82) * mm, "end": v(-16.18, -13.9) * mm});
            skLineSegment(sketch, "E767", {"start": v(-16.18, -13.9) * mm, "end": v(-15.95, -13.99) * mm});
            skLineSegment(sketch, "E768", {"start": v(-15.95, -13.99) * mm, "end": v(-15.74, -14.1) * mm});
            skLineSegment(sketch, "E769", {"start": v(-15.74, -14.1) * mm, "end": v(-15.53, -14.25) * mm});
            skLineSegment(sketch, "E770", {"start": v(-15.53, -14.25) * mm, "end": v(-15.35, -14.43) * mm});
            skLineSegment(sketch, "E771", {"start": v(-15.35, -14.43) * mm, "end": v(-15.2, -14.63) * mm});
            skLineSegment(sketch, "E772", {"start": v(-15.2, -14.63) * mm, "end": v(-15.08, -14.85) * mm});
            skLineSegment(sketch, "E773", {"start": v(-15.08, -14.85) * mm, "end": v(-14.98, -15.09) * mm});
            skLineSegment(sketch, "E774", {"start": v(-14.98, -15.09) * mm, "end": v(-14.92, -15.34) * mm});
            skLineSegment(sketch, "E775", {"start": v(-14.92, -15.34) * mm, "end": v(-14.89, -15.6) * mm});
            skLineSegment(sketch, "E776", {"start": v(-14.89, -15.6) * mm, "end": v(-14.9, -15.88) * mm});
            skLineSegment(sketch, "E777", {"start": v(-14.9, -15.88) * mm, "end": v(-14.96, -16.38) * mm});
            skLineSegment(sketch, "E778", {"start": v(-14.96, -16.38) * mm, "end": v(-15.08, -17.1) * mm});
            skLineSegment(sketch, "E779", {"start": v(-15.08, -17.1) * mm, "end": v(-15.25, -17.95) * mm});
            skLineSegment(sketch, "E780", {"start": v(-15.25, -17.95) * mm, "end": v(-15.43, -18.89) * mm});
            skLineSegment(sketch, "E781", {"start": v(-15.43, -18.89) * mm, "end": v(-15.63, -19.83) * mm});
            skLineSegment(sketch, "E782", {"start": v(-15.63, -19.83) * mm, "end": v(-15.82, -20.7) * mm});
            skLineSegment(sketch, "E783", {"start": v(-15.82, -20.7) * mm, "end": v(-15.99, -21.43) * mm});
            skLineSegment(sketch, "E784", {"start": v(-15.99, -21.43) * mm, "end": v(-16.12, -21.96) * mm});
            skLineSegment(sketch, "E785", {"start": v(-16.12, -21.96) * mm, "end": v(-16.21, -22.21) * mm});
            skLineSegment(sketch, "E786", {"start": v(-16.21, -22.21) * mm, "end": v(-16.33, -22.47) * mm});
            skLineSegment(sketch, "E787", {"start": v(-16.33, -22.47) * mm, "end": v(-16.47, -22.71) * mm});
            skLineSegment(sketch, "E788", {"start": v(-16.47, -22.71) * mm, "end": v(-16.64, -22.94) * mm});
            skLineSegment(sketch, "E789", {"start": v(-16.64, -22.94) * mm, "end": v(-16.83, -23.16) * mm});
            skLineSegment(sketch, "E790", {"start": v(-16.83, -23.16) * mm, "end": v(-17.04, -23.37) * mm});
            skLineSegment(sketch, "E791", {"start": v(-17.04, -23.37) * mm, "end": v(-17.26, -23.55) * mm});
            skLineSegment(sketch, "E792", {"start": v(-17.26, -23.55) * mm, "end": v(-17.5, -23.7) * mm});
            skLineSegment(sketch, "E793", {"start": v(-17.5, -23.7) * mm, "end": v(-17.76, -23.85) * mm});
            skLineSegment(sketch, "E794", {"start": v(-17.76, -23.85) * mm, "end": v(-18.03, -23.96) * mm});
            skLineSegment(sketch, "E795", {"start": v(-18.03, -23.96) * mm, "end": v(-18.3, -24.05) * mm});
            skLineSegment(sketch, "E796", {"start": v(-18.3, -24.05) * mm, "end": v(-18.57, -24.12) * mm});
            skLineSegment(sketch, "E797", {"start": v(-18.57, -24.12) * mm, "end": v(-18.85, -24.17) * mm});
            skLineSegment(sketch, "E798", {"start": v(-18.85, -24.17) * mm, "end": v(-19.12, -24.2) * mm});
            skLineSegment(sketch, "E799", {"start": v(-19.12, -24.2) * mm, "end": v(-19.4, -24.22) * mm});
            skLineSegment(sketch, "E800", {"start": v(-19.4, -24.22) * mm, "end": v(-19.67, -24.22) * mm});
            skLineSegment(sketch, "E801", {"start": v(-19.67, -24.22) * mm, "end": v(-19.9, -24.2) * mm});
            skLineSegment(sketch, "E802", {"start": v(-19.9, -24.2) * mm, "end": v(-20.14, -24.18) * mm});
            skLineSegment(sketch, "E803", {"start": v(-20.14, -24.18) * mm, "end": v(-20.37, -24.14) * mm});
            skLineSegment(sketch, "E804", {"start": v(-20.37, -24.14) * mm, "end": v(-20.6, -24.08) * mm});
            skLineSegment(sketch, "E805", {"start": v(-20.6, -24.08) * mm, "end": v(-20.82, -24) * mm});
            skLineSegment(sketch, "E806", {"start": v(-20.82, -24) * mm, "end": v(-21.02, -23.9) * mm});
            skLineSegment(sketch, "E807", {"start": v(-21.02, -23.9) * mm, "end": v(-21.21, -23.8) * mm});
            skLineSegment(sketch, "E808", {"start": v(-21.21, -23.8) * mm, "end": v(-21.4, -23.66) * mm});
            skLineSegment(sketch, "E809", {"start": v(-21.4, -23.66) * mm, "end": v(-21.56, -23.5) * mm});
            skLineSegment(sketch, "E810", {"start": v(-21.56, -23.5) * mm, "end": v(-21.7, -23.31) * mm});
            skLineSegment(sketch, "E811", {"start": v(-21.7, -23.31) * mm, "end": v(-21.82, -23.11) * mm});
            skLineSegment(sketch, "E812", {"start": v(-21.82, -23.11) * mm, "end": v(-21.9, -22.9) * mm});
            skLineSegment(sketch, "E813", {"start": v(-21.9, -22.9) * mm, "end": v(-21.97, -22.66) * mm});
            skLineSegment(sketch, "E814", {"start": v(-21.97, -22.66) * mm, "end": v(-22, -22.41) * mm});
            skLineSegment(sketch, "E815", {"start": v(-22, -22.41) * mm, "end": v(-22.02, -22.16) * mm});
            skLineSegment(sketch, "E816", {"start": v(-22.02, -22.16) * mm, "end": v(-22, -21.9) * mm});
            skLineSegment(sketch, "E817", {"start": v(-22, -21.9) * mm, "end": v(-21.93, -21.47) * mm});
            skLineSegment(sketch, "E818", {"start": v(-21.93, -21.47) * mm, "end": v(-21.82, -20.85) * mm});
            skLineSegment(sketch, "E819", {"start": v(-21.82, -20.85) * mm, "end": v(-21.68, -20.1) * mm});
            skLineSegment(sketch, "E820", {"start": v(-21.68, -20.1) * mm, "end": v(-21.53, -19.3) * mm});
            skLineSegment(sketch, "E821", {"start": v(-21.53, -19.3) * mm, "end": v(-21.36, -18.49) * mm});
            skLineSegment(sketch, "E822", {"start": v(-21.36, -18.49) * mm, "end": v(-21.2, -17.74) * mm});
            skLineSegment(sketch, "E823", {"start": v(-21.2, -17.74) * mm, "end": v(-21.07, -17.12) * mm});
            skLineSegment(sketch, "E824", {"start": v(-21.07, -17.12) * mm, "end": v(-20.97, -16.68) * mm});
            skLineSegment(sketch, "E825", {"start": v(-20.97, -16.68) * mm, "end": v(-20.93, -16.5) * mm});
            skLineSegment(sketch, "E826", {"start": v(-20.93, -16.5) * mm, "end": v(-20.89, -16.34) * mm});
            skLineSegment(sketch, "E827", {"start": v(-20.89, -16.34) * mm, "end": v(-20.84, -16.17) * mm});
            skLineSegment(sketch, "E828", {"start": v(-20.84, -16.17) * mm, "end": v(-20.8, -16) * mm});
            skLineSegment(sketch, "E829", {"start": v(-20.8, -16) * mm, "end": v(-20.74, -15.84) * mm});
            skLineSegment(sketch, "E830", {"start": v(-20.74, -15.84) * mm, "end": v(-20.68, -15.67) * mm});
            skLineSegment(sketch, "E831", {"start": v(-20.68, -15.67) * mm, "end": v(-20.6, -15.51) * mm});
            skLineSegment(sketch, "E832", {"start": v(-20.6, -15.51) * mm, "end": v(-20.52, -15.35) * mm});
            skLineSegment(sketch, "E833", {"start": v(-20.52, -15.35) * mm, "end": v(-20.38, -15.14) * mm});
            skLineSegment(sketch, "E834", {"start": v(-20.38, -15.14) * mm, "end": v(-20.23, -14.94) * mm});
            skLineSegment(sketch, "E835", {"start": v(-20.23, -14.94) * mm, "end": v(-20.07, -14.75) * mm});
            skLineSegment(sketch, "E836", {"start": v(-20.07, -14.75) * mm, "end": v(-19.89, -14.58) * mm});
            skLineSegment(sketch, "E837", {"start": v(-19.89, -14.58) * mm, "end": v(-19.7, -14.42) * mm});
            skLineSegment(sketch, "E838", {"start": v(-19.7, -14.42) * mm, "end": v(-19.49, -14.27) * mm});
            skLineSegment(sketch, "E839", {"start": v(-19.49, -14.27) * mm, "end": v(-19.27, -14.14) * mm});
            skLineSegment(sketch, "E840", {"start": v(-19.27, -14.14) * mm, "end": v(-19.05, -14.04) * mm});
            skLineSegment(sketch, "E841", {"start": v(-19.05, -14.04) * mm, "end": v(-18.88, -13.97) * mm});
            skLineSegment(sketch, "E842", {"start": v(-18.88, -13.97) * mm, "end": v(-18.72, -13.9) * mm});
            skLineSegment(sketch, "E843", {"start": v(-18.72, -13.9) * mm, "end": v(-18.55, -13.86) * mm});
            skLineSegment(sketch, "E844", {"start": v(-18.55, -13.86) * mm, "end": v(-18.38, -13.81) * mm});
            skLineSegment(sketch, "E845", {"start": v(-18.38, -13.81) * mm, "end": v(-18.22, -13.78) * mm});
            skLineSegment(sketch, "E846", {"start": v(-18.22, -13.78) * mm, "end": v(-18.05, -13.75) * mm});
            skLineSegment(sketch, "E847", {"start": v(-18.05, -13.75) * mm, "end": v(-17.88, -13.73) * mm});
            skLineSegment(sketch, "E848", {"start": v(-17.88, -13.73) * mm, "end": v(-17.72, -13.72) * mm});
            skLineSegment(sketch, "E849", {"start": v(-18.06, -15.64) * mm, "end": v(-18.1, -15.74) * mm});
            skLineSegment(sketch, "E850", {"start": v(-18.1, -15.74) * mm, "end": v(-18.14, -15.83) * mm});
            skLineSegment(sketch, "E851", {"start": v(-18.14, -15.83) * mm, "end": v(-18.17, -15.93) * mm});
            skLineSegment(sketch, "E852", {"start": v(-18.17, -15.93) * mm, "end": v(-18.2, -16.03) * mm});
            skLineSegment(sketch, "E853", {"start": v(-18.2, -16.03) * mm, "end": v(-18.22, -16.12) * mm});
            skLineSegment(sketch, "E854", {"start": v(-18.22, -16.12) * mm, "end": v(-18.24, -16.22) * mm});
            skLineSegment(sketch, "E855", {"start": v(-18.24, -16.22) * mm, "end": v(-18.26, -16.32) * mm});
            skLineSegment(sketch, "E856", {"start": v(-18.26, -16.32) * mm, "end": v(-18.29, -16.41) * mm});
            skLineSegment(sketch, "E857", {"start": v(-18.29, -16.41) * mm, "end": v(-18.41, -17.03) * mm});
            skLineSegment(sketch, "E858", {"start": v(-18.41, -17.03) * mm, "end": v(-18.54, -17.65) * mm});
            skLineSegment(sketch, "E859", {"start": v(-18.54, -17.65) * mm, "end": v(-18.67, -18.27) * mm});
            skLineSegment(sketch, "E860", {"start": v(-18.67, -18.27) * mm, "end": v(-18.8, -18.9) * mm});
            skLineSegment(sketch, "E861", {"start": v(-18.8, -18.9) * mm, "end": v(-18.92, -19.51) * mm});
            skLineSegment(sketch, "E862", {"start": v(-18.92, -19.51) * mm, "end": v(-19.04, -20.13) * mm});
            skLineSegment(sketch, "E863", {"start": v(-19.04, -20.13) * mm, "end": v(-19.17, -20.75) * mm});
            skLineSegment(sketch, "E864", {"start": v(-19.17, -20.75) * mm, "end": v(-19.3, -21.38) * mm});
            skLineSegment(sketch, "E865", {"start": v(-19.3, -21.38) * mm, "end": v(-19.32, -21.5) * mm});
            skLineSegment(sketch, "E866", {"start": v(-19.32, -21.5) * mm, "end": v(-19.34, -21.6) * mm});
            skLineSegment(sketch, "E867", {"start": v(-19.34, -21.6) * mm, "end": v(-19.36, -21.72) * mm});
            skLineSegment(sketch, "E868", {"start": v(-19.36, -21.72) * mm, "end": v(-19.38, -21.84) * mm});
            skLineSegment(sketch, "E869", {"start": v(-19.38, -21.84) * mm, "end": v(-19.4, -21.95) * mm});
            skLineSegment(sketch, "E870", {"start": v(-19.4, -21.95) * mm, "end": v(-19.41, -22.07) * mm});
            skLineSegment(sketch, "E871", {"start": v(-19.41, -22.07) * mm, "end": v(-19.42, -22.18) * mm});
            skLineSegment(sketch, "E872", {"start": v(-19.42, -22.18) * mm, "end": v(-19.42, -22.3) * mm});
            skLineSegment(sketch, "E873", {"start": v(-19.42, -22.3) * mm, "end": v(-19.4, -22.38) * mm});
            skLineSegment(sketch, "E874", {"start": v(-19.4, -22.38) * mm, "end": v(-19.35, -22.45) * mm});
            skLineSegment(sketch, "E875", {"start": v(-19.35, -22.45) * mm, "end": v(-19.27, -22.48) * mm});
            skLineSegment(sketch, "E876", {"start": v(-19.27, -22.48) * mm, "end": v(-19.18, -22.5) * mm});
            skLineSegment(sketch, "E877", {"start": v(-19.18, -22.5) * mm, "end": v(-19.08, -22.48) * mm});
            skLineSegment(sketch, "E878", {"start": v(-19.08, -22.48) * mm, "end": v(-19, -22.44) * mm});
            skLineSegment(sketch, "E879", {"start": v(-19, -22.44) * mm, "end": v(-18.91, -22.38) * mm});
            skLineSegment(sketch, "E880", {"start": v(-18.91, -22.38) * mm, "end": v(-18.85, -22.3) * mm});
            skLineSegment(sketch, "E881", {"start": v(-18.85, -22.3) * mm, "end": v(-18.81, -22.2) * mm});
            skLineSegment(sketch, "E882", {"start": v(-18.81, -22.2) * mm, "end": v(-18.77, -22.09) * mm});
            skLineSegment(sketch, "E883", {"start": v(-18.77, -22.09) * mm, "end": v(-18.74, -21.99) * mm});
            skLineSegment(sketch, "E884", {"start": v(-18.74, -21.99) * mm, "end": v(-18.71, -21.88) * mm});
            skLineSegment(sketch, "E885", {"start": v(-18.71, -21.88) * mm, "end": v(-18.69, -21.78) * mm});
            skLineSegment(sketch, "E886", {"start": v(-18.69, -21.78) * mm, "end": v(-18.66, -21.67) * mm});
            skLineSegment(sketch, "E887", {"start": v(-18.66, -21.67) * mm, "end": v(-18.64, -21.57) * mm});
            skLineSegment(sketch, "E888", {"start": v(-18.64, -21.57) * mm, "end": v(-18.61, -21.46) * mm});
            skLineSegment(sketch, "E889", {"start": v(-18.61, -21.46) * mm, "end": v(-18.48, -20.81) * mm});
            skLineSegment(sketch, "E890", {"start": v(-18.48, -20.81) * mm, "end": v(-18.35, -20.17) * mm});
            skLineSegment(sketch, "E891", {"start": v(-18.35, -20.17) * mm, "end": v(-18.21, -19.52) * mm});
            skLineSegment(sketch, "E892", {"start": v(-18.21, -19.52) * mm, "end": v(-18.08, -18.87) * mm});
            skLineSegment(sketch, "E893", {"start": v(-18.08, -18.87) * mm, "end": v(-17.95, -18.22) * mm});
            skLineSegment(sketch, "E894", {"start": v(-17.95, -18.22) * mm, "end": v(-17.82, -17.58) * mm});
            skLineSegment(sketch, "E895", {"start": v(-17.82, -17.58) * mm, "end": v(-17.69, -16.93) * mm});
            skLineSegment(sketch, "E896", {"start": v(-17.69, -16.93) * mm, "end": v(-17.55, -16.28) * mm});
            skLineSegment(sketch, "E897", {"start": v(-17.55, -16.28) * mm, "end": v(-17.54, -16.2) * mm});
            skLineSegment(sketch, "E898", {"start": v(-17.54, -16.2) * mm, "end": v(-17.53, -16.12) * mm});
            skLineSegment(sketch, "E899", {"start": v(-17.53, -16.12) * mm, "end": v(-17.51, -16.03) * mm});
            skLineSegment(sketch, "E900", {"start": v(-17.51, -16.03) * mm, "end": v(-17.5, -15.95) * mm});
            skLineSegment(sketch, "E901", {"start": v(-17.5, -15.95) * mm, "end": v(-17.5, -15.87) * mm});
            skLineSegment(sketch, "E902", {"start": v(-17.5, -15.87) * mm, "end": v(-17.49, -15.78) * mm});
            skLineSegment(sketch, "E903", {"start": v(-17.49, -15.78) * mm, "end": v(-17.48, -15.7) * mm});
            skLineSegment(sketch, "E904", {"start": v(-17.48, -15.7) * mm, "end": v(-17.49, -15.62) * mm});
            skLineSegment(sketch, "E905", {"start": v(-17.49, -15.62) * mm, "end": v(-17.5, -15.57) * mm});
            skLineSegment(sketch, "E906", {"start": v(-17.5, -15.57) * mm, "end": v(-17.51, -15.52) * mm});
            skLineSegment(sketch, "E907", {"start": v(-17.51, -15.52) * mm, "end": v(-17.55, -15.49) * mm});
            skLineSegment(sketch, "E908", {"start": v(-17.55, -15.49) * mm, "end": v(-17.59, -15.46) * mm});
            skLineSegment(sketch, "E909", {"start": v(-17.59, -15.46) * mm, "end": v(-17.64, -15.44) * mm});
            skLineSegment(sketch, "E910", {"start": v(-17.64, -15.44) * mm, "end": v(-17.7, -15.44) * mm});
            skLineSegment(sketch, "E911", {"start": v(-17.7, -15.44) * mm, "end": v(-17.75, -15.44) * mm});
            skLineSegment(sketch, "E912", {"start": v(-17.75, -15.44) * mm, "end": v(-17.8, -15.44) * mm});
            skLineSegment(sketch, "E913", {"start": v(-17.8, -15.44) * mm, "end": v(-17.84, -15.45) * mm});
            skLineSegment(sketch, "E914", {"start": v(-17.84, -15.45) * mm, "end": v(-17.88, -15.47) * mm});
            skLineSegment(sketch, "E915", {"start": v(-17.88, -15.47) * mm, "end": v(-17.92, -15.49) * mm});
            skLineSegment(sketch, "E916", {"start": v(-17.92, -15.49) * mm, "end": v(-17.95, -15.51) * mm});
            skLineSegment(sketch, "E917", {"start": v(-17.95, -15.51) * mm, "end": v(-17.99, -15.54) * mm});
            skLineSegment(sketch, "E918", {"start": v(-17.99, -15.54) * mm, "end": v(-18.02, -15.57) * mm});
            skLineSegment(sketch, "E919", {"start": v(-18.02, -15.57) * mm, "end": v(-18.04, -15.6) * mm});
            skLineSegment(sketch, "E920", {"start": v(-18.04, -15.6) * mm, "end": v(-18.06, -15.64) * mm});
            skLineSegment(sketch, "E921", {"start": v(-26.84, -13.92) * mm, "end": v(-26.5, -13.92) * mm});
            skLineSegment(sketch, "E922", {"start": v(-26.5, -13.92) * mm, "end": v(-26.17, -13.92) * mm});
            skLineSegment(sketch, "E923", {"start": v(-26.17, -13.92) * mm, "end": v(-25.83, -13.92) * mm});
            skLineSegment(sketch, "E924", {"start": v(-25.83, -13.92) * mm, "end": v(-25.5, -13.92) * mm});
            skLineSegment(sketch, "E925", {"start": v(-25.5, -13.92) * mm, "end": v(-25.16, -13.92) * mm});
            skLineSegment(sketch, "E926", {"start": v(-25.16, -13.92) * mm, "end": v(-24.82, -13.92) * mm});
            skLineSegment(sketch, "E927", {"start": v(-24.82, -13.92) * mm, "end": v(-24.48, -13.92) * mm});
            skLineSegment(sketch, "E928", {"start": v(-24.48, -13.92) * mm, "end": v(-24.14, -13.93) * mm});
            skLineSegment(sketch, "E929", {"start": v(-24.14, -13.93) * mm, "end": v(-23.96, -13.94) * mm});
            skLineSegment(sketch, "E930", {"start": v(-23.96, -13.94) * mm, "end": v(-23.78, -13.95) * mm});
            skLineSegment(sketch, "E931", {"start": v(-23.78, -13.95) * mm, "end": v(-23.6, -13.96) * mm});
            skLineSegment(sketch, "E932", {"start": v(-23.6, -13.96) * mm, "end": v(-23.42, -13.97) * mm});
            skLineSegment(sketch, "E933", {"start": v(-23.42, -13.97) * mm, "end": v(-23.25, -13.99) * mm});
            skLineSegment(sketch, "E934", {"start": v(-23.25, -13.99) * mm, "end": v(-23.07, -14) * mm});
            skLineSegment(sketch, "E935", {"start": v(-23.07, -14) * mm, "end": v(-22.9, -14.03) * mm});
            skLineSegment(sketch, "E936", {"start": v(-22.9, -14.03) * mm, "end": v(-22.72, -14.07) * mm});
            skLineSegment(sketch, "E937", {"start": v(-22.72, -14.07) * mm, "end": v(-22.58, -14.1) * mm});
            skLineSegment(sketch, "E938", {"start": v(-22.58, -14.1) * mm, "end": v(-22.45, -14.16) * mm});
            skLineSegment(sketch, "E939", {"start": v(-22.45, -14.16) * mm, "end": v(-22.32, -14.21) * mm});
            skLineSegment(sketch, "E940", {"start": v(-22.32, -14.21) * mm, "end": v(-22.2, -14.28) * mm});
            skLineSegment(sketch, "E941", {"start": v(-22.2, -14.28) * mm, "end": v(-22.08, -14.36) * mm});
            skLineSegment(sketch, "E942", {"start": v(-22.08, -14.36) * mm, "end": v(-21.98, -14.45) * mm});
            skLineSegment(sketch, "E943", {"start": v(-21.98, -14.45) * mm, "end": v(-21.89, -14.55) * mm});
            skLineSegment(sketch, "E944", {"start": v(-21.89, -14.55) * mm, "end": v(-21.81, -14.67) * mm});
            skLineSegment(sketch, "E945", {"start": v(-21.81, -14.67) * mm, "end": v(-21.76, -14.76) * mm});
            skLineSegment(sketch, "E946", {"start": v(-21.76, -14.76) * mm, "end": v(-21.73, -14.85) * mm});
            skLineSegment(sketch, "E947", {"start": v(-21.73, -14.85) * mm, "end": v(-21.7, -14.95) * mm});
            skLineSegment(sketch, "E948", {"start": v(-21.7, -14.95) * mm, "end": v(-21.67, -15.05) * mm});
            skLineSegment(sketch, "E949", {"start": v(-21.67, -15.05) * mm, "end": v(-21.65, -15.16) * mm});
            skLineSegment(sketch, "E950", {"start": v(-21.65, -15.16) * mm, "end": v(-21.64, -15.27) * mm});
            skLineSegment(sketch, "E951", {"start": v(-21.64, -15.27) * mm, "end": v(-21.64, -15.38) * mm});
            skLineSegment(sketch, "E952", {"start": v(-21.64, -15.38) * mm, "end": v(-21.64, -15.49) * mm});
            skLineSegment(sketch, "E953", {"start": v(-21.64, -15.49) * mm, "end": v(-21.66, -15.72) * mm});
            skLineSegment(sketch, "E954", {"start": v(-21.66, -15.72) * mm, "end": v(-21.7, -15.96) * mm});
            skLineSegment(sketch, "E955", {"start": v(-21.7, -15.96) * mm, "end": v(-21.73, -16.2) * mm});
            skLineSegment(sketch, "E956", {"start": v(-21.73, -16.2) * mm, "end": v(-21.77, -16.43) * mm});
            skLineSegment(sketch, "E957", {"start": v(-21.77, -16.43) * mm, "end": v(-21.82, -16.67) * mm});
            skLineSegment(sketch, "E958", {"start": v(-21.82, -16.67) * mm, "end": v(-21.87, -16.91) * mm});
            skLineSegment(sketch, "E959", {"start": v(-21.87, -16.91) * mm, "end": v(-21.92, -17.15) * mm});
            skLineSegment(sketch, "E960", {"start": v(-21.92, -17.15) * mm, "end": v(-21.96, -17.39) * mm});
            skLineSegment(sketch, "E961", {"start": v(-21.96, -17.39) * mm, "end": v(-22, -17.58) * mm});
            skLineSegment(sketch, "E962", {"start": v(-22, -17.58) * mm, "end": v(-22.04, -17.77) * mm});
            skLineSegment(sketch, "E963", {"start": v(-22.04, -17.77) * mm, "end": v(-22.09, -17.97) * mm});
            skLineSegment(sketch, "E964", {"start": v(-22.09, -17.97) * mm, "end": v(-22.14, -18.16) * mm});
            skLineSegment(sketch, "E965", {"start": v(-22.14, -18.16) * mm, "end": v(-22.2, -18.35) * mm});
            skLineSegment(sketch, "E966", {"start": v(-22.2, -18.35) * mm, "end": v(-22.26, -18.54) * mm});
            skLineSegment(sketch, "E967", {"start": v(-22.26, -18.54) * mm, "end": v(-22.34, -18.73) * mm});
            skLineSegment(sketch, "E968", {"start": v(-22.34, -18.73) * mm, "end": v(-22.43, -18.92) * mm});
            skLineSegment(sketch, "E969", {"start": v(-22.43, -18.92) * mm, "end": v(-22.52, -19.06) * mm});
            skLineSegment(sketch, "E970", {"start": v(-22.52, -19.06) * mm, "end": v(-22.62, -19.19) * mm});
            skLineSegment(sketch, "E971", {"start": v(-22.62, -19.19) * mm, "end": v(-22.74, -19.3) * mm});
            skLineSegment(sketch, "E972", {"start": v(-22.74, -19.3) * mm, "end": v(-22.87, -19.41) * mm});
            skLineSegment(sketch, "E973", {"start": v(-22.87, -19.41) * mm, "end": v(-23, -19.5) * mm});
            skLineSegment(sketch, "E974", {"start": v(-23, -19.5) * mm, "end": v(-23.15, -19.59) * mm});
            skLineSegment(sketch, "E975", {"start": v(-23.15, -19.59) * mm, "end": v(-23.3, -19.66) * mm});
            skLineSegment(sketch, "E976", {"start": v(-23.3, -19.66) * mm, "end": v(-23.45, -19.72) * mm});
            skLineSegment(sketch, "E977", {"start": v(-23.45, -19.72) * mm, "end": v(-23.71, -19.8) * mm});
            skLineSegment(sketch, "E978", {"start": v(-23.71, -19.8) * mm, "end": v(-23.97, -19.85) * mm});
            skLineSegment(sketch, "E979", {"start": v(-23.97, -19.85) * mm, "end": v(-24.24, -19.88) * mm});
            skLineSegment(sketch, "E980", {"start": v(-24.24, -19.88) * mm, "end": v(-24.5, -19.9) * mm});
            skLineSegment(sketch, "E981", {"start": v(-24.5, -19.9) * mm, "end": v(-24.76, -19.9) * mm});
            skLineSegment(sketch, "E982", {"start": v(-24.76, -19.9) * mm, "end": v(-25.02, -19.9) * mm});
            skLineSegment(sketch, "E983", {"start": v(-25.02, -19.9) * mm, "end": v(-25.27, -19.9) * mm});
            skLineSegment(sketch, "E984", {"start": v(-25.27, -19.9) * mm, "end": v(-25.53, -19.9) * mm});
            skLineSegment(sketch, "E985", {"start": v(-25.53, -19.9) * mm, "end": v(-25.64, -20.42) * mm});
            skLineSegment(sketch, "E986", {"start": v(-25.64, -20.42) * mm, "end": v(-25.74, -20.93) * mm});
            skLineSegment(sketch, "E987", {"start": v(-25.74, -20.93) * mm, "end": v(-25.85, -21.45) * mm});
            skLineSegment(sketch, "E988", {"start": v(-25.85, -21.45) * mm, "end": v(-25.95, -21.96) * mm});
            skLineSegment(sketch, "E989", {"start": v(-25.95, -21.96) * mm, "end": v(-26.06, -22.47) * mm});
            skLineSegment(sketch, "E990", {"start": v(-26.06, -22.47) * mm, "end": v(-26.16, -22.99) * mm});
            skLineSegment(sketch, "E991", {"start": v(-26.16, -22.99) * mm, "end": v(-26.27, -23.5) * mm});
            skLineSegment(sketch, "E992", {"start": v(-26.27, -23.5) * mm, "end": v(-26.37, -24.01) * mm});
            skLineSegment(sketch, "E993", {"start": v(-26.37, -24.01) * mm, "end": v(-26.69, -24.01) * mm});
            skLineSegment(sketch, "E994", {"start": v(-26.69, -24.01) * mm, "end": v(-27, -24.01) * mm});
            skLineSegment(sketch, "E995", {"start": v(-27, -24.01) * mm, "end": v(-27.32, -24.01) * mm});
            skLineSegment(sketch, "E996", {"start": v(-27.32, -24.01) * mm, "end": v(-27.64, -24.01) * mm});
            skLineSegment(sketch, "E997", {"start": v(-27.64, -24.01) * mm, "end": v(-27.95, -24.01) * mm});
            skLineSegment(sketch, "E998", {"start": v(-27.95, -24.01) * mm, "end": v(-28.27, -24.01) * mm});
            skLineSegment(sketch, "E999", {"start": v(-28.27, -24.01) * mm, "end": v(-28.59, -24.01) * mm});
            skLineSegment(sketch, "E1000", {"start": v(-28.59, -24.01) * mm, "end": v(-28.9, -24.01) * mm});
            skLineSegment(sketch, "E1001", {"start": v(-28.9, -24.01) * mm, "end": v(-28.65, -22.75) * mm});
            skLineSegment(sketch, "E1002", {"start": v(-28.65, -22.75) * mm, "end": v(-28.4, -21.5) * mm});
            skLineSegment(sketch, "E1003", {"start": v(-28.4, -21.5) * mm, "end": v(-28.13, -20.23) * mm});
            skLineSegment(sketch, "E1004", {"start": v(-28.13, -20.23) * mm, "end": v(-27.88, -18.97) * mm});
            skLineSegment(sketch, "E1005", {"start": v(-27.88, -18.97) * mm, "end": v(-27.62, -17.7) * mm});
            skLineSegment(sketch, "E1006", {"start": v(-27.62, -17.7) * mm, "end": v(-27.36, -16.45) * mm});
            skLineSegment(sketch, "E1007", {"start": v(-27.36, -16.45) * mm, "end": v(-27.1, -15.18) * mm});
            skLineSegment(sketch, "E1008", {"start": v(-27.1, -15.18) * mm, "end": v(-26.84, -13.92) * mm});
            skLineSegment(sketch, "E1009", {"start": v(-25.05, -18.17) * mm, "end": v(-24.97, -18.16) * mm});
            skLineSegment(sketch, "E1010", {"start": v(-24.97, -18.16) * mm, "end": v(-24.88, -18.16) * mm});
            skLineSegment(sketch, "E1011", {"start": v(-24.88, -18.16) * mm, "end": v(-24.78, -18.15) * mm});
            skLineSegment(sketch, "E1012", {"start": v(-24.78, -18.15) * mm, "end": v(-24.7, -18.14) * mm});
            skLineSegment(sketch, "E1013", {"start": v(-24.7, -18.14) * mm, "end": v(-24.6, -18.11) * mm});
            skLineSegment(sketch, "E1014", {"start": v(-24.6, -18.11) * mm, "end": v(-24.52, -18.07) * mm});
            skLineSegment(sketch, "E1015", {"start": v(-24.52, -18.07) * mm, "end": v(-24.44, -18.01) * mm});
            skLineSegment(sketch, "E1016", {"start": v(-24.44, -18.01) * mm, "end": v(-24.38, -17.93) * mm});
            skLineSegment(sketch, "E1017", {"start": v(-24.38, -17.93) * mm, "end": v(-24.3, -17.76) * mm});
            skLineSegment(sketch, "E1018", {"start": v(-24.3, -17.76) * mm, "end": v(-24.22, -17.52) * mm});
            skLineSegment(sketch, "E1019", {"start": v(-24.22, -17.52) * mm, "end": v(-24.14, -17.22) * mm});
            skLineSegment(sketch, "E1020", {"start": v(-24.14, -17.22) * mm, "end": v(-24.07, -16.9) * mm});
            skLineSegment(sketch, "E1021", {"start": v(-24.07, -16.9) * mm, "end": v(-24.01, -16.58) * mm});
            skLineSegment(sketch, "E1022", {"start": v(-24.01, -16.58) * mm, "end": v(-23.97, -16.28) * mm});
            skLineSegment(sketch, "E1023", {"start": v(-23.97, -16.28) * mm, "end": v(-23.96, -16.04) * mm});
            skLineSegment(sketch, "E1024", {"start": v(-23.96, -16.04) * mm, "end": v(-23.97, -15.87) * mm});
            skLineSegment(sketch, "E1025", {"start": v(-23.97, -15.87) * mm, "end": v(-24.02, -15.8) * mm});
            skLineSegment(sketch, "E1026", {"start": v(-24.02, -15.8) * mm, "end": v(-24.08, -15.76) * mm});
            skLineSegment(sketch, "E1027", {"start": v(-24.08, -15.76) * mm, "end": v(-24.14, -15.73) * mm});
            skLineSegment(sketch, "E1028", {"start": v(-24.14, -15.73) * mm, "end": v(-24.22, -15.7) * mm});
            skLineSegment(sketch, "E1029", {"start": v(-24.22, -15.7) * mm, "end": v(-24.3, -15.7) * mm});
            skLineSegment(sketch, "E1030", {"start": v(-24.3, -15.7) * mm, "end": v(-24.39, -15.68) * mm});
            skLineSegment(sketch, "E1031", {"start": v(-24.39, -15.68) * mm, "end": v(-24.47, -15.68) * mm});
            skLineSegment(sketch, "E1032", {"start": v(-24.47, -15.68) * mm, "end": v(-24.55, -15.67) * mm});
            skLineSegment(sketch, "E1033", {"start": v(-24.55, -15.67) * mm, "end": v(-24.61, -15.98) * mm});
            skLineSegment(sketch, "E1034", {"start": v(-24.61, -15.98) * mm, "end": v(-24.68, -16.3) * mm});
            skLineSegment(sketch, "E1035", {"start": v(-24.68, -16.3) * mm, "end": v(-24.74, -16.6) * mm});
            skLineSegment(sketch, "E1036", {"start": v(-24.74, -16.6) * mm, "end": v(-24.8, -16.92) * mm});
            skLineSegment(sketch, "E1037", {"start": v(-24.8, -16.92) * mm, "end": v(-24.87, -17.23) * mm});
            skLineSegment(sketch, "E1038", {"start": v(-24.87, -17.23) * mm, "end": v(-24.93, -17.54) * mm});
            skLineSegment(sketch, "E1039", {"start": v(-24.93, -17.54) * mm, "end": v(-25, -17.85) * mm});
            skLineSegment(sketch, "E1040", {"start": v(-25, -17.85) * mm, "end": v(-25.05, -18.17) * mm});
            skLineSegment(sketch, "E1041", {"start": v(-2.92, -13.06) * mm, "end": v(-2.5, -13.06) * mm});
            skLineSegment(sketch, "E1042", {"start": v(-2.5, -13.06) * mm, "end": v(-2.07, -13.06) * mm});
            skLineSegment(sketch, "E1043", {"start": v(-2.07, -13.06) * mm, "end": v(-1.65, -13.06) * mm});
            skLineSegment(sketch, "E1044", {"start": v(-1.65, -13.06) * mm, "end": v(-1.23, -13.06) * mm});
            skLineSegment(sketch, "E1045", {"start": v(-1.23, -13.06) * mm, "end": v(-0.8, -13.06) * mm});
            skLineSegment(sketch, "E1046", {"start": v(-0.8, -13.06) * mm, "end": v(-0.38, -13.06) * mm});
            skLineSegment(sketch, "E1047", {"start": v(-0.38, -13.06) * mm, "end": v(0.06, -13.06) * mm});
            skLineSegment(sketch, "E1048", {"start": v(0.06, -13.06) * mm, "end": v(0.5, -13.06) * mm});
            skLineSegment(sketch, "E1049", {"start": v(0.5, -13.06) * mm, "end": v(0.4, -13.57) * mm});
            skLineSegment(sketch, "E1050", {"start": v(0.4, -13.57) * mm, "end": v(0.22, -14.4) * mm});
            skLineSegment(sketch, "E1051", {"start": v(0.22, -14.4) * mm, "end": v(0, -15.49) * mm});
            skLineSegment(sketch, "E1052", {"start": v(0, -15.49) * mm, "end": v(-0.27, -16.77) * mm});
            skLineSegment(sketch, "E1053", {"start": v(-0.27, -16.77) * mm, "end": v(-0.57, -18.19) * mm});
            skLineSegment(sketch, "E1054", {"start": v(-0.57, -18.19) * mm, "end": v(-0.88, -19.67) * mm});
            skLineSegment(sketch, "E1055", {"start": v(-0.88, -19.67) * mm, "end": v(-1.19, -21.17) * mm});
            skLineSegment(sketch, "E1056", {"start": v(-1.19, -21.17) * mm, "end": v(-1.48, -22.6) * mm});
            skLineSegment(sketch, "E1057", {"start": v(-1.48, -22.6) * mm, "end": v(-1.2, -22.6) * mm});
            skLineSegment(sketch, "E1058", {"start": v(-1.2, -22.6) * mm, "end": v(-0.91, -22.6) * mm});
            skLineSegment(sketch, "E1059", {"start": v(-0.91, -22.6) * mm, "end": v(-0.63, -22.61) * mm});
            skLineSegment(sketch, "E1060", {"start": v(-0.63, -22.61) * mm, "end": v(-0.35, -22.61) * mm});
            skLineSegment(sketch, "E1061", {"start": v(-0.35, -22.61) * mm, "end": v(-0.07, -22.62) * mm});
            skLineSegment(sketch, "E1062", {"start": v(-0.07, -22.62) * mm, "end": v(0.2, -22.62) * mm});
            skLineSegment(sketch, "E1063", {"start": v(0.2, -22.62) * mm, "end": v(0.47, -22.62) * mm});
            skLineSegment(sketch, "E1064", {"start": v(0.47, -22.62) * mm, "end": v(0.74, -22.62) * mm});
            skLineSegment(sketch, "E1065", {"start": v(0.74, -22.62) * mm, "end": v(0.68, -22.91) * mm});
            skLineSegment(sketch, "E1066", {"start": v(0.68, -22.91) * mm, "end": v(0.62, -23.2) * mm});
            skLineSegment(sketch, "E1067", {"start": v(0.62, -23.2) * mm, "end": v(0.56, -23.48) * mm});
            skLineSegment(sketch, "E1068", {"start": v(0.56, -23.48) * mm, "end": v(0.5, -23.76) * mm});
            skLineSegment(sketch, "E1069", {"start": v(0.5, -23.76) * mm, "end": v(0.45, -24.03) * mm});
            skLineSegment(sketch, "E1070", {"start": v(0.45, -24.03) * mm, "end": v(0.4, -24.3) * mm});
            skLineSegment(sketch, "E1071", {"start": v(0.4, -24.3) * mm, "end": v(0.34, -24.58) * mm});
            skLineSegment(sketch, "E1072", {"start": v(0.34, -24.58) * mm, "end": v(0.28, -24.86) * mm});
            skLineSegment(sketch, "E1073", {"start": v(0.28, -24.86) * mm, "end": v(-0.44, -24.86) * mm});
            skLineSegment(sketch, "E1074", {"start": v(-0.44, -24.86) * mm, "end": v(-1.18, -24.86) * mm});
            skLineSegment(sketch, "E1075", {"start": v(-1.18, -24.86) * mm, "end": v(-1.93, -24.86) * mm});
            skLineSegment(sketch, "E1076", {"start": v(-1.93, -24.86) * mm, "end": v(-2.68, -24.86) * mm});
            skLineSegment(sketch, "E1077", {"start": v(-2.68, -24.86) * mm, "end": v(-3.4, -24.86) * mm});
            skLineSegment(sketch, "E1078", {"start": v(-3.4, -24.86) * mm, "end": v(-4.1, -24.86) * mm});
            skLineSegment(sketch, "E1079", {"start": v(-4.1, -24.86) * mm, "end": v(-4.75, -24.86) * mm});
            skLineSegment(sketch, "E1080", {"start": v(-4.75, -24.86) * mm, "end": v(-5.33, -24.86) * mm});
            skLineSegment(sketch, "E1081", {"start": v(-5.33, -24.86) * mm, "end": v(-5.09, -23.69) * mm});
            skLineSegment(sketch, "E1082", {"start": v(-5.09, -23.69) * mm, "end": v(-4.77, -22.13) * mm});
            skLineSegment(sketch, "E1083", {"start": v(-4.77, -22.13) * mm, "end": v(-4.4, -20.34) * mm});
            skLineSegment(sketch, "E1084", {"start": v(-4.4, -20.34) * mm, "end": v(-4.02, -18.47) * mm});
            skLineSegment(sketch, "E1085", {"start": v(-4.02, -18.47) * mm, "end": v(-3.65, -16.66) * mm});
            skLineSegment(sketch, "E1086", {"start": v(-3.65, -16.66) * mm, "end": v(-3.32, -15.05) * mm});
            skLineSegment(sketch, "E1087", {"start": v(-3.32, -15.05) * mm, "end": v(-3.07, -13.8) * mm});
            skLineSegment(sketch, "E1088", {"start": v(-3.07, -13.8) * mm, "end": v(-2.92, -13.06) * mm});
            skLineSegment(sketch, "E1089", {"start": v(5.11, -13.07) * mm, "end": v(5.74, -13.07) * mm});
            skLineSegment(sketch, "E1090", {"start": v(5.74, -13.07) * mm, "end": v(6.37, -13.07) * mm});
            skLineSegment(sketch, "E1091", {"start": v(6.37, -13.07) * mm, "end": v(7, -13.07) * mm});
            skLineSegment(sketch, "E1092", {"start": v(7, -13.07) * mm, "end": v(7.63, -13.07) * mm});
            skLineSegment(sketch, "E1093", {"start": v(7.63, -13.07) * mm, "end": v(8.25, -13.07) * mm});
            skLineSegment(sketch, "E1094", {"start": v(8.25, -13.07) * mm, "end": v(8.88, -13.07) * mm});
            skLineSegment(sketch, "E1095", {"start": v(8.88, -13.07) * mm, "end": v(9.51, -13.07) * mm});
            skLineSegment(sketch, "E1096", {"start": v(9.51, -13.07) * mm, "end": v(10.14, -13.07) * mm});
            skLineSegment(sketch, "E1097", {"start": v(10.14, -13.07) * mm, "end": v(10.1, -14.46) * mm});
            skLineSegment(sketch, "E1098", {"start": v(10.1, -14.46) * mm, "end": v(10.05, -15.85) * mm});
            skLineSegment(sketch, "E1099", {"start": v(10.05, -15.85) * mm, "end": v(10, -17.25) * mm});
            skLineSegment(sketch, "E1100", {"start": v(10, -17.25) * mm, "end": v(9.96, -18.64) * mm});
            skLineSegment(sketch, "E1101", {"start": v(9.96, -18.64) * mm, "end": v(9.92, -20.04) * mm});
            skLineSegment(sketch, "E1102", {"start": v(9.92, -20.04) * mm, "end": v(9.87, -21.43) * mm});
            skLineSegment(sketch, "E1103", {"start": v(9.87, -21.43) * mm, "end": v(9.82, -22.82) * mm});
            skLineSegment(sketch, "E1104", {"start": v(9.82, -22.82) * mm, "end": v(9.78, -24.22) * mm});
            skLineSegment(sketch, "E1105", {"start": v(9.78, -24.22) * mm, "end": v(9.78, -24.3) * mm});
            skLineSegment(sketch, "E1106", {"start": v(9.78, -24.3) * mm, "end": v(9.77, -24.38) * mm});
            skLineSegment(sketch, "E1107", {"start": v(9.77, -24.38) * mm, "end": v(9.77, -24.46) * mm});
            skLineSegment(sketch, "E1108", {"start": v(9.77, -24.46) * mm, "end": v(9.77, -24.54) * mm});
            skLineSegment(sketch, "E1109", {"start": v(9.77, -24.54) * mm, "end": v(9.77, -24.63) * mm});
            skLineSegment(sketch, "E1110", {"start": v(9.77, -24.63) * mm, "end": v(9.76, -24.7) * mm});
            skLineSegment(sketch, "E1111", {"start": v(9.76, -24.7) * mm, "end": v(9.76, -24.79) * mm});
            skLineSegment(sketch, "E1112", {"start": v(9.76, -24.79) * mm, "end": v(9.75, -24.87) * mm});
            skLineSegment(sketch, "E1113", {"start": v(9.75, -24.87) * mm, "end": v(9.32, -24.87) * mm});
            skLineSegment(sketch, "E1114", {"start": v(9.32, -24.87) * mm, "end": v(8.88, -24.87) * mm});
            skLineSegment(sketch, "E1115", {"start": v(8.88, -24.87) * mm, "end": v(8.44, -24.87) * mm});
            skLineSegment(sketch, "E1116", {"start": v(8.44, -24.87) * mm, "end": v(8, -24.87) * mm});
            skLineSegment(sketch, "E1117", {"start": v(8, -24.87) * mm, "end": v(7.57, -24.87) * mm});
            skLineSegment(sketch, "E1118", {"start": v(7.57, -24.87) * mm, "end": v(7.13, -24.87) * mm});
            skLineSegment(sketch, "E1119", {"start": v(7.13, -24.87) * mm, "end": v(6.7, -24.87) * mm});
            skLineSegment(sketch, "E1120", {"start": v(6.7, -24.87) * mm, "end": v(6.26, -24.86) * mm});
            skLineSegment(sketch, "E1121", {"start": v(6.26, -24.86) * mm, "end": v(6.29, -24.6) * mm});
            skLineSegment(sketch, "E1122", {"start": v(6.29, -24.6) * mm, "end": v(6.32, -24.33) * mm});
            skLineSegment(sketch, "E1123", {"start": v(6.32, -24.33) * mm, "end": v(6.35, -24.06) * mm});
            skLineSegment(sketch, "E1124", {"start": v(6.35, -24.06) * mm, "end": v(6.38, -23.8) * mm});
            skLineSegment(sketch, "E1125", {"start": v(6.38, -23.8) * mm, "end": v(6.41, -23.53) * mm});
            skLineSegment(sketch, "E1126", {"start": v(6.41, -23.53) * mm, "end": v(6.44, -23.26) * mm});
            skLineSegment(sketch, "E1127", {"start": v(6.44, -23.26) * mm, "end": v(6.47, -23) * mm});
            skLineSegment(sketch, "E1128", {"start": v(6.47, -23) * mm, "end": v(6.5, -22.73) * mm});
            skLineSegment(sketch, "E1129", {"start": v(6.5, -22.73) * mm, "end": v(6.35, -22.73) * mm});
            skLineSegment(sketch, "E1130", {"start": v(6.35, -22.73) * mm, "end": v(6.19, -22.73) * mm});
            skLineSegment(sketch, "E1131", {"start": v(6.19, -22.73) * mm, "end": v(6.02, -22.73) * mm});
            skLineSegment(sketch, "E1132", {"start": v(6.02, -22.73) * mm, "end": v(5.85, -22.73) * mm});
            skLineSegment(sketch, "E1133", {"start": v(5.85, -22.73) * mm, "end": v(5.67, -22.73) * mm});
            skLineSegment(sketch, "E1134", {"start": v(5.67, -22.73) * mm, "end": v(5.5, -22.73) * mm});
            skLineSegment(sketch, "E1135", {"start": v(5.5, -22.73) * mm, "end": v(5.3, -22.73) * mm});
            skLineSegment(sketch, "E1136", {"start": v(5.3, -22.73) * mm, "end": v(5.1, -22.73) * mm});
            skLineSegment(sketch, "E1137", {"start": v(5.1, -22.73) * mm, "end": v(5.02, -23) * mm});
            skLineSegment(sketch, "E1138", {"start": v(5.02, -23) * mm, "end": v(4.94, -23.28) * mm});
            skLineSegment(sketch, "E1139", {"start": v(4.94, -23.28) * mm, "end": v(4.85, -23.55) * mm});
            skLineSegment(sketch, "E1140", {"start": v(4.85, -23.55) * mm, "end": v(4.78, -23.81) * mm});
            skLineSegment(sketch, "E1141", {"start": v(4.78, -23.81) * mm, "end": v(4.7, -24.08) * mm});
            skLineSegment(sketch, "E1142", {"start": v(4.7, -24.08) * mm, "end": v(4.62, -24.34) * mm});
            skLineSegment(sketch, "E1143", {"start": v(4.62, -24.34) * mm, "end": v(4.54, -24.6) * mm});
            skLineSegment(sketch, "E1144", {"start": v(4.54, -24.6) * mm, "end": v(4.46, -24.86) * mm});
            skLineSegment(sketch, "E1145", {"start": v(4.46, -24.86) * mm, "end": v(4, -24.86) * mm});
            skLineSegment(sketch, "E1146", {"start": v(4, -24.86) * mm, "end": v(3.54, -24.86) * mm});
            skLineSegment(sketch, "E1147", {"start": v(3.54, -24.86) * mm, "end": v(3.08, -24.86) * mm});
            skLineSegment(sketch, "E1148", {"start": v(3.08, -24.86) * mm, "end": v(2.63, -24.86) * mm});
            skLineSegment(sketch, "E1149", {"start": v(2.63, -24.86) * mm, "end": v(2.2, -24.86) * mm});
            skLineSegment(sketch, "E1150", {"start": v(2.2, -24.86) * mm, "end": v(1.76, -24.87) * mm});
            skLineSegment(sketch, "E1151", {"start": v(1.76, -24.87) * mm, "end": v(1.34, -24.87) * mm});
            skLineSegment(sketch, "E1152", {"start": v(1.34, -24.87) * mm, "end": v(0.92, -24.87) * mm});
            skLineSegment(sketch, "E1153", {"start": v(0.92, -24.87) * mm, "end": v(1.44, -23.4) * mm});
            skLineSegment(sketch, "E1154", {"start": v(1.44, -23.4) * mm, "end": v(1.97, -21.92) * mm});
            skLineSegment(sketch, "E1155", {"start": v(1.97, -21.92) * mm, "end": v(2.5, -20.44) * mm});
            skLineSegment(sketch, "E1156", {"start": v(2.5, -20.44) * mm, "end": v(3.02, -18.97) * mm});
            skLineSegment(sketch, "E1157", {"start": v(3.02, -18.97) * mm, "end": v(3.54, -17.5) * mm});
            skLineSegment(sketch, "E1158", {"start": v(3.54, -17.5) * mm, "end": v(4.07, -16.02) * mm});
            skLineSegment(sketch, "E1159", {"start": v(4.07, -16.02) * mm, "end": v(4.6, -14.54) * mm});
            skLineSegment(sketch, "E1160", {"start": v(4.6, -14.54) * mm, "end": v(5.11, -13.07) * mm});
            skLineSegment(sketch, "E1161", {"start": v(5.73, -20.47) * mm, "end": v(5.79, -20.47) * mm});
            skLineSegment(sketch, "E1162", {"start": v(5.79, -20.47) * mm, "end": v(5.9, -20.47) * mm});
            skLineSegment(sketch, "E1163", {"start": v(5.9, -20.47) * mm, "end": v(6.07, -20.47) * mm});
            skLineSegment(sketch, "E1164", {"start": v(6.07, -20.47) * mm, "end": v(6.26, -20.47) * mm});
            skLineSegment(sketch, "E1165", {"start": v(6.26, -20.47) * mm, "end": v(6.45, -20.47) * mm});
            skLineSegment(sketch, "E1166", {"start": v(6.45, -20.47) * mm, "end": v(6.62, -20.47) * mm});
            skLineSegment(sketch, "E1167", {"start": v(6.62, -20.47) * mm, "end": v(6.74, -20.47) * mm});
            skLineSegment(sketch, "E1168", {"start": v(6.74, -20.47) * mm, "end": v(6.8, -20.47) * mm});
            skLineSegment(sketch, "E1169", {"start": v(6.8, -20.47) * mm, "end": v(6.81, -20.23) * mm});
            skLineSegment(sketch, "E1170", {"start": v(6.81, -20.23) * mm, "end": v(6.86, -19.73) * mm});
            skLineSegment(sketch, "E1171", {"start": v(6.86, -19.73) * mm, "end": v(6.93, -19.04) * mm});
            skLineSegment(sketch, "E1172", {"start": v(6.93, -19.04) * mm, "end": v(7, -18.25) * mm});
            skLineSegment(sketch, "E1173", {"start": v(7, -18.25) * mm, "end": v(7.08, -17.47) * mm});
            skLineSegment(sketch, "E1174", {"start": v(7.08, -17.47) * mm, "end": v(7.14, -16.77) * mm});
            skLineSegment(sketch, "E1175", {"start": v(7.14, -16.77) * mm, "end": v(7.2, -16.25) * mm});
            skLineSegment(sketch, "E1176", {"start": v(7.2, -16.25) * mm, "end": v(7.22, -16) * mm});
            skLineSegment(sketch, "E1177", {"start": v(7.22, -16) * mm, "end": v(7.15, -16.2) * mm});
            skLineSegment(sketch, "E1178", {"start": v(7.15, -16.2) * mm, "end": v(7, -16.68) * mm});
            skLineSegment(sketch, "E1179", {"start": v(7, -16.68) * mm, "end": v(6.77, -17.35) * mm});
            skLineSegment(sketch, "E1180", {"start": v(6.77, -17.35) * mm, "end": v(6.51, -18.11) * mm});
            skLineSegment(sketch, "E1181", {"start": v(6.51, -18.11) * mm, "end": v(6.25, -18.9) * mm});
            skLineSegment(sketch, "E1182", {"start": v(6.25, -18.9) * mm, "end": v(6.02, -19.6) * mm});
            skLineSegment(sketch, "E1183", {"start": v(6.02, -19.6) * mm, "end": v(5.83, -20.16) * mm});
            skLineSegment(sketch, "E1184", {"start": v(5.83, -20.16) * mm, "end": v(5.73, -20.47) * mm});
            skLineSegment(sketch, "E1185", {"start": v(22.8, -14.95) * mm, "end": v(23.23, -14.9) * mm});
            skLineSegment(sketch, "E1186", {"start": v(23.23, -14.9) * mm, "end": v(23.66, -14.9) * mm});
            skLineSegment(sketch, "E1187", {"start": v(23.66, -14.9) * mm, "end": v(24.07, -14.9) * mm});
            skLineSegment(sketch, "E1188", {"start": v(24.07, -14.9) * mm, "end": v(24.48, -14.95) * mm});
            skLineSegment(sketch, "E1189", {"start": v(24.48, -14.95) * mm, "end": v(24.88, -15.03) * mm});
            skLineSegment(sketch, "E1190", {"start": v(24.88, -15.03) * mm, "end": v(25.26, -15.14) * mm});
            skLineSegment(sketch, "E1191", {"start": v(25.26, -15.14) * mm, "end": v(25.63, -15.28) * mm});
            skLineSegment(sketch, "E1192", {"start": v(25.63, -15.28) * mm, "end": v(25.98, -15.46) * mm});
            skLineSegment(sketch, "E1193", {"start": v(25.98, -15.46) * mm, "end": v(26.22, -15.6) * mm});
            skLineSegment(sketch, "E1194", {"start": v(26.22, -15.6) * mm, "end": v(26.45, -15.77) * mm});
            skLineSegment(sketch, "E1195", {"start": v(26.45, -15.77) * mm, "end": v(26.66, -15.96) * mm});
            skLineSegment(sketch, "E1196", {"start": v(26.66, -15.96) * mm, "end": v(26.85, -16.16) * mm});
            skLineSegment(sketch, "E1197", {"start": v(26.85, -16.16) * mm, "end": v(27.03, -16.38) * mm});
            skLineSegment(sketch, "E1198", {"start": v(27.03, -16.38) * mm, "end": v(27.19, -16.6) * mm});
            skLineSegment(sketch, "E1199", {"start": v(27.19, -16.6) * mm, "end": v(27.32, -16.86) * mm});
            skLineSegment(sketch, "E1200", {"start": v(27.32, -16.86) * mm, "end": v(27.43, -17.12) * mm});
            skLineSegment(sketch, "E1201", {"start": v(27.43, -17.12) * mm, "end": v(27.52, -17.43) * mm});
            skLineSegment(sketch, "E1202", {"start": v(27.52, -17.43) * mm, "end": v(27.58, -17.76) * mm});
            skLineSegment(sketch, "E1203", {"start": v(27.58, -17.76) * mm, "end": v(27.6, -18.1) * mm});
            skLineSegment(sketch, "E1204", {"start": v(27.6, -18.1) * mm, "end": v(27.57, -18.43) * mm});
            skLineSegment(sketch, "E1205", {"start": v(27.57, -18.43) * mm, "end": v(27.51, -18.78) * mm});
            skLineSegment(sketch, "E1206", {"start": v(27.51, -18.78) * mm, "end": v(27.42, -19.12) * mm});
            skLineSegment(sketch, "E1207", {"start": v(27.42, -19.12) * mm, "end": v(27.29, -19.46) * mm});
            skLineSegment(sketch, "E1208", {"start": v(27.29, -19.46) * mm, "end": v(27.12, -19.8) * mm});
            skLineSegment(sketch, "E1209", {"start": v(27.12, -19.8) * mm, "end": v(26.96, -20.06) * mm});
            skLineSegment(sketch, "E1210", {"start": v(26.96, -20.06) * mm, "end": v(26.77, -20.3) * mm});
            skLineSegment(sketch, "E1211", {"start": v(26.77, -20.3) * mm, "end": v(26.58, -20.55) * mm});
            skLineSegment(sketch, "E1212", {"start": v(26.58, -20.55) * mm, "end": v(26.36, -20.78) * mm});
            skLineSegment(sketch, "E1213", {"start": v(26.36, -20.78) * mm, "end": v(26.14, -21) * mm});
            skLineSegment(sketch, "E1214", {"start": v(26.14, -21) * mm, "end": v(25.9, -21.2) * mm});
            skLineSegment(sketch, "E1215", {"start": v(25.9, -21.2) * mm, "end": v(25.64, -21.39) * mm});
            skLineSegment(sketch, "E1216", {"start": v(25.64, -21.39) * mm, "end": v(25.39, -21.56) * mm});
            skLineSegment(sketch, "E1217", {"start": v(25.39, -21.56) * mm, "end": v(24.75, -21.91) * mm});
            skLineSegment(sketch, "E1218", {"start": v(24.75, -21.91) * mm, "end": v(24.1, -22.19) * mm});
            skLineSegment(sketch, "E1219", {"start": v(24.1, -22.19) * mm, "end": v(23.43, -22.38) * mm});
            skLineSegment(sketch, "E1220", {"start": v(23.43, -22.38) * mm, "end": v(22.76, -22.5) * mm});
            skLineSegment(sketch, "E1221", {"start": v(22.76, -22.5) * mm, "end": v(22.1, -22.53) * mm});
            skLineSegment(sketch, "E1222", {"start": v(22.1, -22.53) * mm, "end": v(21.44, -22.5) * mm});
            skLineSegment(sketch, "E1223", {"start": v(21.44, -22.5) * mm, "end": v(20.81, -22.37) * mm});
            skLineSegment(sketch, "E1224", {"start": v(20.81, -22.37) * mm, "end": v(20.22, -22.18) * mm});
            skLineSegment(sketch, "E1225", {"start": v(20.22, -22.18) * mm, "end": v(19.93, -22.04) * mm});
            skLineSegment(sketch, "E1226", {"start": v(19.93, -22.04) * mm, "end": v(19.65, -21.89) * mm});
            skLineSegment(sketch, "E1227", {"start": v(19.65, -21.89) * mm, "end": v(19.38, -21.7) * mm});
            skLineSegment(sketch, "E1228", {"start": v(19.38, -21.7) * mm, "end": v(19.13, -21.5) * mm});
            skLineSegment(sketch, "E1229", {"start": v(19.13, -21.5) * mm, "end": v(18.91, -21.27) * mm});
            skLineSegment(sketch, "E1230", {"start": v(18.91, -21.27) * mm, "end": v(18.71, -21.03) * mm});
            skLineSegment(sketch, "E1231", {"start": v(18.71, -21.03) * mm, "end": v(18.54, -20.76) * mm});
            skLineSegment(sketch, "E1232", {"start": v(18.54, -20.76) * mm, "end": v(18.4, -20.47) * mm});
            skLineSegment(sketch, "E1233", {"start": v(18.4, -20.47) * mm, "end": v(18.32, -20.27) * mm});
            skLineSegment(sketch, "E1234", {"start": v(18.32, -20.27) * mm, "end": v(18.25, -20.06) * mm});
            skLineSegment(sketch, "E1235", {"start": v(18.25, -20.06) * mm, "end": v(18.2, -19.85) * mm});
            skLineSegment(sketch, "E1236", {"start": v(18.2, -19.85) * mm, "end": v(18.18, -19.63) * mm});
            skLineSegment(sketch, "E1237", {"start": v(18.18, -19.63) * mm, "end": v(18.17, -19.4) * mm});
            skLineSegment(sketch, "E1238", {"start": v(18.17, -19.4) * mm, "end": v(18.17, -19.18) * mm});
            skLineSegment(sketch, "E1239", {"start": v(18.17, -19.18) * mm, "end": v(18.19, -18.95) * mm});
            skLineSegment(sketch, "E1240", {"start": v(18.19, -18.95) * mm, "end": v(18.22, -18.72) * mm});
            skLineSegment(sketch, "E1241", {"start": v(18.22, -18.72) * mm, "end": v(18.3, -18.44) * mm});
            skLineSegment(sketch, "E1242", {"start": v(18.3, -18.44) * mm, "end": v(18.4, -18.16) * mm});
            skLineSegment(sketch, "E1243", {"start": v(18.4, -18.16) * mm, "end": v(18.5, -17.89) * mm});
            skLineSegment(sketch, "E1244", {"start": v(18.5, -17.89) * mm, "end": v(18.65, -17.62) * mm});
            skLineSegment(sketch, "E1245", {"start": v(18.65, -17.62) * mm, "end": v(18.8, -17.36) * mm});
            skLineSegment(sketch, "E1246", {"start": v(18.8, -17.36) * mm, "end": v(18.98, -17.11) * mm});
            skLineSegment(sketch, "E1247", {"start": v(18.98, -17.11) * mm, "end": v(19.18, -16.87) * mm});
            skLineSegment(sketch, "E1248", {"start": v(19.18, -16.87) * mm, "end": v(19.4, -16.65) * mm});
            skLineSegment(sketch, "E1249", {"start": v(19.4, -16.65) * mm, "end": v(19.76, -16.3) * mm});
            skLineSegment(sketch, "E1250", {"start": v(19.76, -16.3) * mm, "end": v(20.15, -16) * mm});
            skLineSegment(sketch, "E1251", {"start": v(20.15, -16) * mm, "end": v(20.56, -15.74) * mm});
            skLineSegment(sketch, "E1252", {"start": v(20.56, -15.74) * mm, "end": v(21, -15.51) * mm});
            skLineSegment(sketch, "E1253", {"start": v(21, -15.51) * mm, "end": v(21.44, -15.32) * mm});
            skLineSegment(sketch, "E1254", {"start": v(21.44, -15.32) * mm, "end": v(21.9, -15.16) * mm});
            skLineSegment(sketch, "E1255", {"start": v(21.9, -15.16) * mm, "end": v(22.35, -15.04) * mm});
            skLineSegment(sketch, "E1256", {"start": v(22.35, -15.04) * mm, "end": v(22.8, -14.95) * mm});
            skSolve(sketch);
        }
        {
            var Q0;
            Q0=makeQuery(id+"F2.imprint","IMPRINT",FACE,{"disambiguationData":[TD([[makeQuery(id+"F2.imprint","IMPRINT",EDGE,{"derivedFrom":sQuery(id+"F2.wireOp",EDGE,"E921")}),-1.0]])]});
            var Q1;
            Q1=makeQuery(id+"F2.imprint","IMPRINT",FACE,{"disambiguationData":[TD([[makeQuery(id+"F2.imprint","IMPRINT",EDGE,{"derivedFrom":sQuery(id+"F2.wireOp",EDGE,"E761")}),-1.0]])]});
            var Q2;
            Q2=makeQuery(id+"F2.imprint","IMPRINT",FACE,{"disambiguationData":[TD([[makeQuery(id+"F2.imprint","IMPRINT",EDGE,{"derivedFrom":sQuery(id+"F2.wireOp",EDGE,"E713")}),-1.0]])]});
            var Q3;
            Q3=makeQuery(id+"F2.imprint","IMPRINT",FACE,{"disambiguationData":[TD([[makeQuery(id+"F2.imprint","IMPRINT",EDGE,{"derivedFrom":sQuery(id+"F2.wireOp",EDGE,"E633")}),-1.0]])]});
            extrude(context, id + "F3", {"entities" : qUnion([Q0, Q1, Q2, Q3]), "operationType" : NewBodyOperationType.ADD, "depth" : 2 * mm, "offsetDistance" : 25 * mm});
        }
        {
            var Q0;
            {var subQ9=sQuery(id+"F2.wireOp",EDGE,"E82");Q0=makeQuery(id+"F2.imprint","IMPRINT",FACE,{"disambiguationData":[TD([[makeQuery(id+"F2.imprint","IMPRINT",EDGE,{"derivedFrom":subQ9}),1.0]])]});}
            var Q1;
            {var subQ5=sQuery(id+"F2.wireOp",EDGE,"E13");Q1=makeQuery(id+"F2.imprint","IMPRINT",FACE,{"disambiguationData":[TD([[makeQuery(id+"F2.imprint","IMPRINT",EDGE,{"derivedFrom":subQ5}),1.0]])]});}
            var Q2;
            Q2=makeQuery(id+"F2.imprint","IMPRINT",FACE,{"disambiguationData":[TD([[makeQuery(id+"F2.imprint","IMPRINT",EDGE,{"derivedFrom":sQuery(id+"F2.wireOp",EDGE,"E537")}),-1.0]])]});
            var Q3;
            {var subQ5=sQuery(id+"F2.wireOp",EDGE,"E82");Q3=makeQuery(id+"F2.imprint","IMPRINT",FACE,{"disambiguationData":[TD([[makeQuery(id+"F2.imprint","IMPRINT",EDGE,{"derivedFrom":subQ5}),-1.0]])]});}
            var Q4;
            {var subQ0=sQuery(id+"F2.wireOp",EDGE,"E138");Q4=makeQuery(id+"F2.imprint","IMPRINT",FACE,{"disambiguationData":[TD([[makeQuery(id+"F2.imprint","IMPRINT",EDGE,{"derivedFrom":subQ0}),-1.0]])]});}
            var Q5;
            {var subQ1=sQuery(id+"F2.wireOp",EDGE,"E13");Q5=makeQuery(id+"F2.imprint","IMPRINT",FACE,{"disambiguationData":[TD([[makeQuery(id+"F2.imprint","IMPRINT",EDGE,{"derivedFrom":subQ1}),-1.0]])]});}
            extrude(context, id + "F4", {"entities" : qUnion([Q0, Q1, Q2, Q3, Q4, Q5]), "operationType" : NewBodyOperationType.ADD, "depth" : 2.4 * mm, "offsetDistance" : 25 * mm});
        }
        {
            var Q0;
            {var subQ0=sQuery(id+"F2.wireOp",EDGE,"E49");Q0=makeQuery(id+"F2.imprint","IMPRINT",FACE,{"disambiguationData":[TD([[makeQuery(id+"F2.imprint","IMPRINT",EDGE,{"derivedFrom":subQ0}),-1.0]])]});}
            extrude(context, id + "F5", {"entities" : qUnion([Q0]), "operationType" : NewBodyOperationType.ADD, "depth" : 3 * mm, "offsetDistance" : 25 * mm});
        }
        {
            var Q0;
            Q0=makeQuery(id+"F2.imprint","IMPRINT",FACE,{"disambiguationData":[TD([[makeQuery(id+"F2.imprint","IMPRINT",EDGE,{"derivedFrom":sQuery(id+"F2.wireOp",EDGE,"E1")}),-1.0]])]});
            var Q1;
            Q1=makeQuery(id+"F2.imprint","IMPRINT",FACE,{"disambiguationData":[TD([[makeQuery(id+"F2.imprint","IMPRINT",EDGE,{"derivedFrom":sQuery(id+"F2.wireOp",EDGE,"E89")}),-1.0]])]});
            extrude(context, id + "F6", {"entities" : qUnion([Q0, Q1]), "operationType" : NewBodyOperationType.ADD, "depth" : 3.2 * mm, "offsetDistance" : 25 * mm});
        }
        {
            var Q0;
            Q0=makeQuery(id+"F2.imprint","IMPRINT",FACE,{"disambiguationData":[TD([[makeQuery(id+"F2.imprint","IMPRINT",EDGE,{"derivedFrom":sQuery(id+"F2.wireOp",EDGE,"E281")}),-1.0]])]});
            var Q1;
            Q1=makeQuery(id+"F2.imprint","IMPRINT",FACE,{"disambiguationData":[TD([[makeQuery(id+"F2.imprint","IMPRINT",EDGE,{"derivedFrom":sQuery(id+"F2.wireOp",EDGE,"E409")}),-1.0]])]});
            extrude(context, id + "F7", {"entities" : qUnion([Q0, Q1]), "operationType" : NewBodyOperationType.ADD, "depth" : 3.4 * mm, "offsetDistance" : 25 * mm});
        }
        {
            var Q0;
            Q0=makeQuery(id+"F2.imprint","IMPRINT",FACE,{"disambiguationData":[TD([[makeQuery(id+"F2.imprint","IMPRINT",EDGE,{"derivedFrom":sQuery(id+"F2.wireOp",EDGE,"E153")}),-1.0]])]});
            var Q1;
            Q1=makeQuery(id+"F2.imprint","IMPRINT",FACE,{"disambiguationData":[TD([[makeQuery(id+"F2.imprint","IMPRINT",EDGE,{"derivedFrom":sQuery(id+"F2.wireOp",EDGE,"E473")}),-1.0]])]});
            extrude(context, id + "F8", {"entities" : qUnion([Q0, Q1]), "operationType" : NewBodyOperationType.ADD, "depth" : 3.6 * mm, "offsetDistance" : 25 * mm});
        }
        {
            var Q0;
            Q0=makeQuery(id+"F2.imprint","IMPRINT",FACE,{"disambiguationData":[TD([[makeQuery(id+"F2.imprint","IMPRINT",EDGE,{"derivedFrom":sQuery(id+"F2.wireOp",EDGE,"E217")}),-1.0]])]});
            var Q1;
            Q1=makeQuery(id+"F2.imprint","IMPRINT",FACE,{"disambiguationData":[TD([[makeQuery(id+"F2.imprint","IMPRINT",EDGE,{"derivedFrom":sQuery(id+"F2.wireOp",EDGE,"E345")}),-1.0]])]});
            extrude(context, id + "F9", {"entities" : qUnion([Q0, Q1]), "operationType" : NewBodyOperationType.ADD, "depth" : 3.8 * mm, "offsetDistance" : 25 * mm});
        }
        {
            var Q0;
            {var subQ0=sQuery(id+"F2.wireOp",EDGE,"E580");Q0=makeQuery(id+"F2.imprint","IMPRINT",FACE,{"disambiguationData":[TD([[makeQuery(id+"F2.imprint","IMPRINT",EDGE,{"derivedFrom":subQ0}),1.0]])]});}
            var Q1;
            {var subQ4=sQuery(id+"F2.wireOp",EDGE,"E580");Q1=makeQuery(id+"F2.imprint","IMPRINT",FACE,{"disambiguationData":[TD([[makeQuery(id+"F2.imprint","IMPRINT",EDGE,{"derivedFrom":subQ4}),-1.0]])]});}
            extrude(context, id + "F10", {"entities" : qUnion([Q0, Q1]), "operationType" : NewBodyOperationType.ADD, "depth" : 4 * mm, "offsetDistance" : 25 * mm});
        }
        {
            var Q0;
            Q0=makeQuery(id+"F1.opExtrude","SWEPT_EDGE",EDGE,{"disambiguationData":[OSD([sQuery(id+"F0.wireOp",EDGE,"E0.bottom"),sQuery(id+"F0.wireOp",EDGE,"E0.left")])]});
            var Q1;
            Q1=makeQuery(id+"F1.opExtrude","SWEPT_EDGE",EDGE,{"disambiguationData":[OSD([sQuery(id+"F0.wireOp",EDGE,"E0.bottom"),sQuery(id+"F0.wireOp",EDGE,"E0.right")])]});
            var Q2;
            Q2=makeQuery(id+"F1.opExtrude","SWEPT_EDGE",EDGE,{"disambiguationData":[OSD([sQuery(id+"F0.wireOp",EDGE,"E0.top"),sQuery(id+"F0.wireOp",EDGE,"E0.right")])]});
            var Q3;
            Q3=makeQuery(id+"F1.opExtrude","SWEPT_EDGE",EDGE,{"disambiguationData":[OSD([sQuery(id+"F0.wireOp",EDGE,"E0.top"),sQuery(id+"F0.wireOp",EDGE,"E0.left")])]});
            fillet(context, id + "F11", {"entities" : qUnion([Q0, Q1, Q2, Q3]), "radius" : 5 * mm, "tangentPropagation" : true, "allowEdgeOverflow" : false});
        }
        {
            var Q0;
            Q0=makeQuery(id+"F1.opExtrude","CAP_FACE",FACE,{"disambiguationData":[OSD([sQuery(id+"F0.wireOp",EDGE,"E0.bottom"),sQuery(id+"F0.wireOp",EDGE,"E0.top"),sQuery(id+"F0.wireOp",EDGE,"E0.left"),sQuery(id+"F0.wireOp",EDGE,"E0.right")])],"isStart":true});
            chamfer(context, id + "F12", {"entities" : qUnion([Q0]), "width" : 0.5 * mm, "tangentPropagation" : true});
        }
        {
            var Q0;
            Q0=makeQuery(id+"F1.opExtrude","CAP_EDGE",EDGE,{"disambiguationData":[OSD([sQuery(id+"F0.wireOp",EDGE,"E0.left")])],"isStart":false});
            chamfer(context, id + "F13", {"entities" : qUnion([Q0]), "width" : 0.5 * mm, "tangentPropagation" : true});
        }
    });
